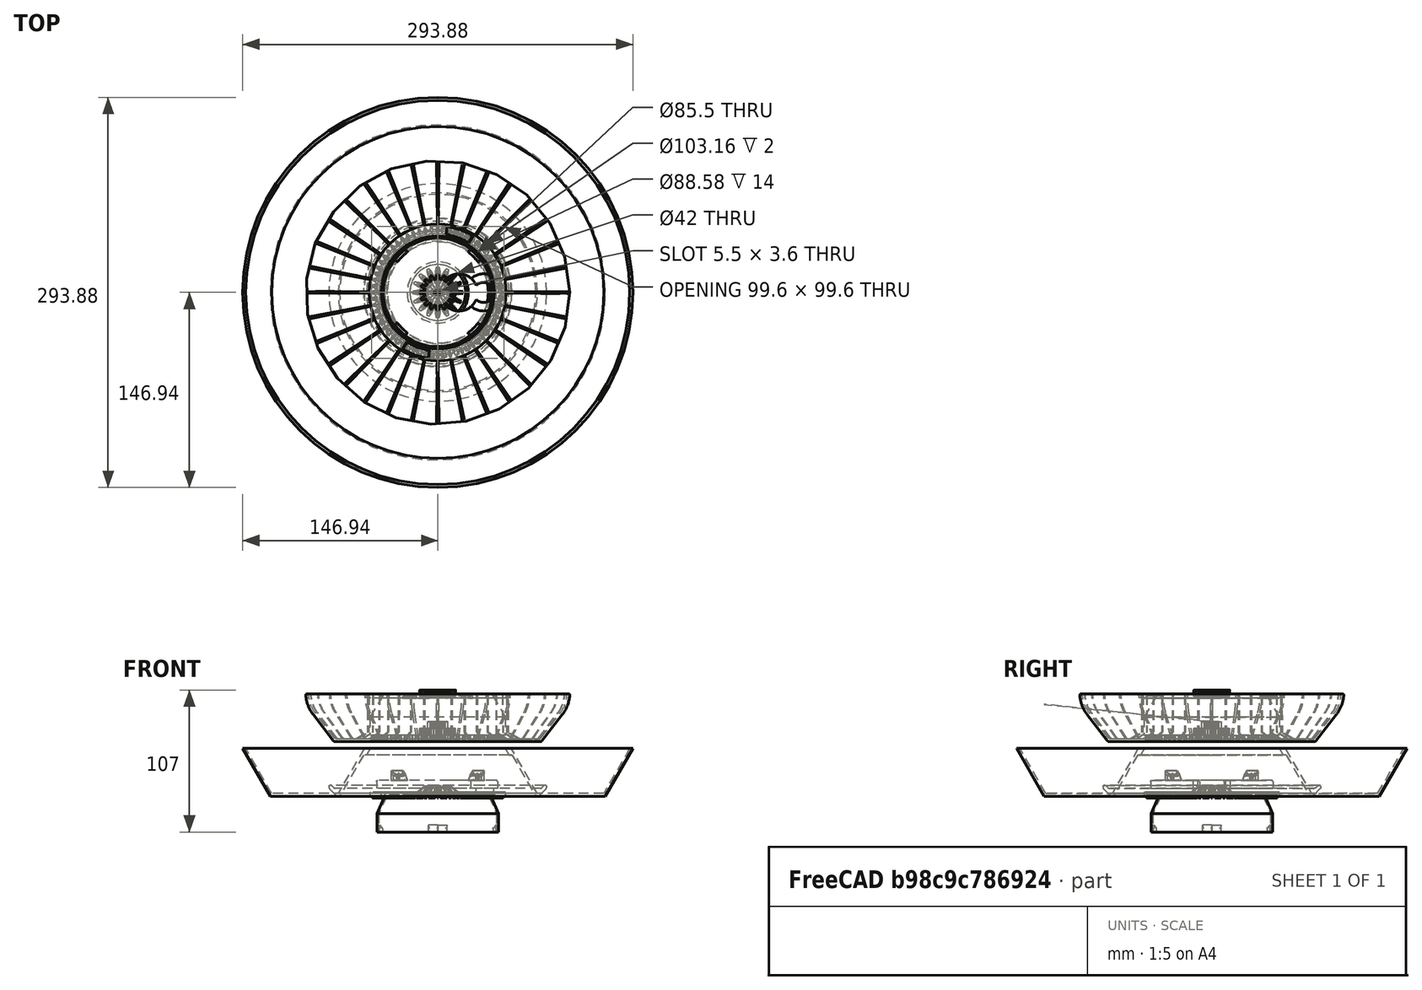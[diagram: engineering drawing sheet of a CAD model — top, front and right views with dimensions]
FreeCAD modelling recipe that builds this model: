
FCSTD DOCUMENT  (FreeCAD 1.1R43087 (Git))
Label: smart_medication_box
License: All rights reserved
LicenseURL: https://en.wikipedia.org/wiki/All_rights_reserved
objects: Sketcher::SketchObject×22, PartDesign::Fillet×13, App::Point×12, PartDesign::Body×11, PartDesign::Pocket×7, PartDesign::Revolution×7, Part::DatumPlane×6, PartDesign::Pad×6, App::Link×6, PartDesign::PolarPattern×5, Measure::MeasureRadius×5, Part::FeaturePython×4, App::FeaturePython×4, Measure::MeasureDistance×4, PartDesign::FeaturePython×3, PartDesign::FeatureBase×2, Mesh::Feature×2, Part::Feature×2, App::VarSet×1, PartDesign::AdditivePipe×1, +8 more types
note: 189 computed .brp shape members not serialized (recipe doc carries the construction recipe); baked Part::Feature solids carry a one-line shape summary decoded from their .brp

FEATURE [App::Point] Origin001
  Role = Origin
FEATURE [Sketcher::SketchObject] Sketch001
  ArcFitTolerance = 1e-06
  ExternalTypes = [0]
  FullyConstrained = true
  MakeInternals = false
  MapMode = 5
  Placement = pos=(0,0,0) rot=(1,0,0;3.14159rad)
  expr: Constraints[10] = 3.1
  expr: Constraints[11] = 2.6
  sketch-geometry (4):
    g0: LineSegment StartX=-1.55 StartY=2.08746 StartZ=0 EndX=-1.55 EndY=-2.08746 EndZ=0
    g1: LineSegment StartX=1.55 StartY=2.08746 StartZ=0 EndX=1.55 EndY=-2.08746 EndZ=0
    g2: ArcOfCircle CenterX=0 CenterY=0 CenterZ=0 NormalX=0 NormalY=0 NormalZ=1 AngleXU=0 Radius=2.6 StartAngle=0.932094 EndAngle=2.2095
    g3: ArcOfCircle CenterX=0 CenterY=0 CenterZ=0 NormalX=0 NormalY=0 NormalZ=1 AngleXU=0 Radius=2.6 StartAngle=4.07369 EndAngle=5.35109
  constraints (12):
    c: Vertical(g1)
    c: Coincident(g2,g-1)
    c: Coincident(g2,g0)
    c: Coincident(g2,g1)
    c: Coincident(g3,g2)
    c: Coincident(g3,g0)
    c: Coincident(g3,g1)
    c: Parallel(g1,g0)
    c: Equal(g1,g0)
    c: Equal(g2,g3)
    c: Distance(g0,g1) = 3.1
    c: Radius(g2) = 2.6
FEATURE [Part::FeaturePython] BevelGear  # WARN: FeaturePython — macro-defined, semantics opaque (R4)
  AttacherType = Attacher::AttachEngine3D
  angular_backlash = 0
  backlash = 0
  beta = 0
  clearance = 0.1
  dw = 32
  height = 7.5
  module = 2
  num_teeth = 16
  numpoints = 20
  pitch_angle = 45
  pressure_angle = 20
  reset_origin = true
  version = 1.3.0
  expr: angular_backlash = backlash / dw * 360 ° / pi
  expr: dw = num_teeth * module
  expr: height = 7.5
  expr: module = 2
  expr: num_teeth = 16
FEATURE [PartDesign::FeatureBase] BaseFeature
  BaseFeature = -> BevelGear
  Suppressed = false
FEATURE [PartDesign::Pocket] Pocket
  BaseFeature = -> BaseFeature
  Direction = (0,0,1)
  Length = 6
  Length2 = 5
  Profile = -> Sketch001
  ReferenceAxis = -> Sketch001 [N_Axis]
  Refine = true
  SideType = 0
  Suppressed = false
  Type = 0
  Type2 = 0
  expr: Length = 6
FEATURE [PartDesign::Body] Body  label="stepper_gear"
  AllowCompound = false
  BaseFeature = -> BevelGear
  Group = -> [BaseFeature,Sketch001,Pocket]
  Origin = -> Origin
  Tip = -> Pocket
FEATURE [App::Point] Origin003
  Role = Origin
FEATURE [Sketcher::SketchObject] Sketch
  ArcFitTolerance = 1e-06
  AttachmentSupport = -> [Origin002]
  ExternalTypes = [0]
  FullyConstrained = true
  MakeInternals = false
  MapMode = 5
  expr: Constraints[1] = 2 * VarSet.outer_ring_center_radius
  sketch-geometry (1):
    g0: Circle CenterX=0 CenterY=0 CenterZ=0 NormalX=0 NormalY=0 NormalZ=1 AngleXU=0 Radius=100
  constraints (2):
    c: Coincident(g0,g-1)
    c: Diameter(g0) = 200
FEATURE [App::VarSet] VarSet
  fillet_oouter_gear = 0.8
  outer_gear_section_length = 48
  outer_ring_bottom_width = 50
  outer_ring_center_radius = 100
  outer_ring_height = 36
  outer_ring_sides_angle = 30
  outer_wall_thickness = 2
  wall_thickness = 2
  expr: fillet_oouter_gear = 0.8
  expr: outer_ring_bottom_width = 50
  expr: outer_ring_center_radius = 100
  expr: outer_ring_height = 36
  expr: outer_ring_sides_angle = 30
FEATURE [Part::DatumPlane] DatumPlane
  AttachmentSupport = -> [Sketch]
  MapMode = 7
  Placement = pos=(100,0,0) rot=(1,0,0;1.5708rad)
FEATURE [Sketcher::SketchObject] Sketch002
  ArcFitTolerance = 1e-06
  AttachmentSupport = -> [DatumPlane]
  ExternalTypes = [0]
  FullyConstrained = true
  MakeInternals = false
  MapMode = 5
  Placement = pos=(100,0,0) rot=(1,0,0;1.5708rad)
  expr: Constraints[13] = VarSet.outer_ring_height
  expr: Constraints[16] = VarSet.outer_ring_sides_angle
  expr: Constraints[17] = VarSet.outer_ring_sides_angle
  expr: Constraints[19] = 5
  expr: Constraints[21] = VarSet.wall_thickness * 2
  expr: Constraints[24] = VarSet.wall_thickness
  expr: Constraints[28] = VarSet.outer_ring_bottom_width
  expr: Constraints[7] = VarSet.wall_thickness
  expr: Constraints[8] = VarSet.outer_ring_height
  expr: Constraints[9] = VarSet.wall_thickness
  sketch-geometry (10):
    g0: LineSegment StartX=26.1547 StartY=0 StartZ=0 EndX=46.9393 EndY=36 EndZ=0
    g1: LineSegment StartX=46.9393 StartY=36 StartZ=0 EndX=44.6299 EndY=36 EndZ=0
    g2: LineSegment StartX=44.6299 StartY=36 StartZ=0 EndX=25 EndY=2 EndZ=0
    g3: LineSegment StartX=25 StartY=2 StartZ=0 EndX=-25 EndY=2 EndZ=0
    g4: LineSegment StartX=-25 StartY=2 StartZ=0 EndX=-44.6299 EndY=36 EndZ=0
    g5: LineSegment StartX=-44.6299 StartY=36 StartZ=0 EndX=-49.2487 EndY=36 EndZ=0
    g6: LineSegment StartX=-26.1547 StartY=0 StartZ=0 EndX=26.1547 EndY=0 EndZ=0
    g7: LineSegment StartX=-49.2487 StartY=36 StartZ=0 EndX=-46.362 EndY=31 EndZ=0
    g8: LineSegment StartX=-44.0526 StartY=31 StartZ=0 EndX=-26.1547 EndY=0 EndZ=0
    g9: LineSegment StartX=-44.0526 StartY=31 StartZ=0 EndX=-46.362 EndY=31 EndZ=0
  constraints (29):
    c: Coincident(g1,g0)
    c: Coincident(g1,g2)
    c: Coincident(g2,g3)
    c: Coincident(g3,g4)
    c: Coincident(g4,g5)
    c: Horizontal(g5)
    c: Coincident(g6,g0)
    c: Distance(g0,g2) = 2
    c: DistanceY(g6,g4) = 36
    c: DistanceY(g6,g3) = 2
    c: Parallel(g3,g6)
    c: Parallel(g1,g-1)
    c: Parallel(g0,g2)
    c: Distance(g-1,g1) = 36
    c: Symmetric(g6,g0,g-2)
    c: PointOnObject(g0,g-1)
    c: Angle(g2,g-2) = 0.523599
    c: Angle(g-2,g4) = 0.523599
    c: Coincident(g7,g5)
    c: DistanceY(g7,g5) = 5
    c: Parallel(g7,g4)
    c: Distance(g4,g7) = 4
    c: Coincident(g8,g6)
    c: Parallel(g8,g4)
    c: Distance(g4,g8) = 2
    c: Coincident(g9,g8)
    c: Coincident(g9,g7)
    c: Parallel(g9,g5)
    c: DistanceX(g3,g3) = 50
FEATURE [PartDesign::AdditivePipe] AdditivePipe
  AuxiliaryCurvilinear = true
  AuxiliarySpineTangent = false
  Binormal = (0,0,0)
  Mode = 0
  Placement = pos=(100,0,0) rot=(1,0,0;1.5708rad)
  Profile = -> Sketch002
  Refine = true
  Spine = -> Sketch
  SpineTangent = false
  Suppressed = false
  Transformation = 0
  Transition = 0
FEATURE [PartDesign::Body] Body001  label="outer_sections_ring_gear"
  AllowCompound = false
  Group = -> [Sketch,DatumPlane,Sketch002,AdditivePipe]
  Origin = -> Origin002
  Tip = -> AdditivePipe
FEATURE [App::Point] Origin005
  Role = Origin
FEATURE [PartDesign::FeaturePython] BevelGear001  # WARN: FeaturePython — macro-defined, semantics opaque (R4)
  AttacherType = Attacher::AttachEngine3D
  Suppressed = false
  angular_backlash = 0
  backlash = 0
  beta = 0
  clearance = 0.1
  dw = 96
  height = 5
  module = 1.5
  num_teeth = 64
  numpoints = 20
  pitch_angle = 30
  pressure_angle = 20
  reset_origin = true
  version = 1.3.0
  expr: angular_backlash = backlash / dw * 360 ° / pi
  expr: dw = num_teeth * module
  expr: module = 1.5
  expr: num_teeth = 64
  expr: pitch_angle = 30
FEATURE [PartDesign::Body] Body002  label="Body"
  AllowCompound = false
  Group = -> [BevelGear001]
  Origin = -> Origin004
  Placement = pos=(0,0,45) rot=(0,0,1;0rad)
  Tip = -> BevelGear001
FEATURE [Part::Cut] Cut
  Base = -> Body001
  Refine = true
  Tool = -> Body002
FEATURE [App::Point] Origin007
  Role = Origin
FEATURE [Sketcher::SketchObject] Sketch003
  ArcFitTolerance = 1e-06
  AttachmentSupport = -> [Origin006]
  ExternalTypes = [0]
  FullyConstrained = true
  MakeInternals = false
  MapMode = 5
  expr: Constraints[0] = 53 * 2
  sketch-geometry (1):
    g0: Circle CenterX=0 CenterY=0 CenterZ=0 NormalX=0 NormalY=0 NormalZ=1 AngleXU=0 Radius=53
  constraints (2):
    c: Diameter(g0) = 106
    c: Coincident(g0,g-1)
FEATURE [PartDesign::Pad] Pad
  Direction = (0,0,1)
  Length = 6
  Length2 = 10
  Profile = -> Sketch003
  ReferenceAxis = -> Sketch003 [N_Axis]
  Refine = true
  SideType = 0
  Suppressed = false
  Type = 0
  Type2 = 0
  expr: Length = 6
FEATURE [Sketcher::SketchObject] Sketch004
  ArcFitTolerance = 1e-06
  AttachmentSupport = -> [Pad]
  ExternalTypes = [0]
  FullyConstrained = true
  MakeInternals = false
  MapMode = 5
  Placement = pos=(0,0,6) rot=(0,0,1;0rad)
  expr: Constraints[0] = 48 * 2 - 4
  sketch-geometry (1):
    g0: Circle CenterX=0 CenterY=0 CenterZ=0 NormalX=0 NormalY=0 NormalZ=1 AngleXU=0 Radius=46
  constraints (2):
    c: Diameter(g0) = 92
    c: Coincident(g0,g-1)
FEATURE [PartDesign::Pad] Pad001
  BaseFeature = -> Pad
  Direction = (0,0,1)
  Length = 6
  Length2 = 10
  Profile = -> Sketch004
  ReferenceAxis = -> Sketch004 [N_Axis]
  Refine = true
  SideType = 0
  Suppressed = false
  Type = 0
  Type2 = 0
  expr: Length = 6
FEATURE [Part::FeaturePython] InvoluteGear  # WARN: FeaturePython — macro-defined, semantics opaque (R4)
  AttacherType = Attacher::AttachEngine3D
  Placement = pos=(0,0,41) rot=(0,0,1;0rad)
  addendum_diameter = 15
  angular_backlash = 0
  axle_hole = false
  axle_holesize = 10
  backlash = 0
  clearance = 0.25
  double_helix = false
  head = 0
  head_fillet = 0
  height = 5
  helix_angle = 0
  module = 1.5
  num_teeth = 8
  numpoints = 20
  offset_hole = false
  offset_holeoffset = 10
  offset_holesize = 10
  pitch_diameter = 12
  pressure_angle = 20
  properties_from_tool = false
  reversed_backlash = false
  root_diameter = 8.25
  root_fillet = 0
  shift = 0
  simple = false
  transverse_pitch = 4.71239
  traverse_module = 1.5
  undercut = false
  version = 1.3.0
  expr: angular_backlash = backlash / pitch_diameter * 360 ° / pi
  expr: module = 1.5
  expr: num_teeth = 8
FEATURE [Sketcher::SketchObject] Sketch005
  ArcFitTolerance = 1e-06
  AttachmentSupport = -> [Pad001]
  ExternalGeometry = -> [Pad001]
  ExternalTypes = [0]
  FullyConstrained = true
  MakeInternals = false
  MapMode = 5
  Placement = pos=(0,0,12) rot=(0,0,1;0rad)
  expr: Constraints[0] = 28
  expr: Constraints[4] = 11.5
  sketch-geometry (2):
    g0: Circle CenterX=34.5 CenterY=0 CenterZ=0 NormalX=0 NormalY=0 NormalZ=1 AngleXU=0 Radius=14
    g1: Circle [constr] CenterX=34.5 CenterY=0 CenterZ=0 NormalX=0 NormalY=0 NormalZ=1 AngleXU=0 Radius=11.5
  constraints (5):
    c: Diameter(g0) = 28
    c: Coincident(g1,g0)
    c: Tangent(g1,g-3)
    c: PointOnObject(g0,g-1)
    c: Distance(g0,g-3) = 11.5
FEATURE [PartDesign::Pocket] Pocket001
  BaseFeature = -> Pad001
  Direction = (0,0,-1)
  Length = 6
  Length2 = 5
  Profile = -> Sketch005
  ReferenceAxis = -> Sketch005 [N_Axis]
  Refine = true
  SideType = 0
  Suppressed = false
  Type = 0
  Type2 = 0
  expr: Length = 6
FEATURE [Sketcher::SketchObject] Sketch006
  ArcFitTolerance = 1e-06
  AttachmentSupport = -> [Pocket001]
  ExternalGeometry = -> [Pocket001]
  ExternalTypes = [0,0]
  FullyConstrained = true
  MakeInternals = false
  MapMode = 5
  Placement = pos=(0,0,6) rot=(0,0,1;0rad)
  sketch-geometry (1):
    g0: Circle CenterX=34.5 CenterY=0 CenterZ=0 NormalX=0 NormalY=0 NormalZ=1 AngleXU=0 Radius=7.6
  constraints (2):
    c: Diameter(g0) = 15.2
    c: Coincident(g0,g-4)
FEATURE [PartDesign::Pocket] Pocket002
  BaseFeature = -> Pocket001
  Direction = (0,0,-1)
  Length = 5
  Length2 = 5
  Profile = -> Sketch006
  ReferenceAxis = -> Sketch006 [N_Axis]
  Refine = true
  SideType = 0
  Suppressed = false
  Type = 0
  Type2 = 0
FEATURE [App::Point] Origin011
  Role = Origin
FEATURE [PartDesign::FeaturePython] InvoluteGear001  # WARN: FeaturePython — macro-defined, semantics opaque (R4)
  AttacherType = Attacher::AttachEngine3D
  Suppressed = false
  addendum_diameter = 27
  angular_backlash = 0
  axle_hole = false
  axle_holesize = 10
  backlash = 0
  clearance = 0.25
  double_helix = false
  head = 0
  head_fillet = 0
  height = 5
  helix_angle = 0
  module = 1.5
  num_teeth = 16
  numpoints = 20
  offset_hole = false
  offset_holeoffset = 10
  offset_holesize = 10
  pitch_diameter = 24
  pressure_angle = 20
  properties_from_tool = false
  reversed_backlash = false
  root_diameter = 20.25
  root_fillet = 0
  shift = 0
  simple = false
  transverse_pitch = 4.71239
  traverse_module = 1.5
  undercut = false
  version = 1.3.0
  expr: angular_backlash = backlash / pitch_diameter * 360 ° / pi
  expr: module = 1.5
  expr: num_teeth = 16
FEATURE [Sketcher::SketchObject] Sketch007
  ArcFitTolerance = 1e-06
  AttachmentSupport = -> [Pocket002]
  ExternalGeometry = -> [Pocket002]
  ExternalTypes = [0]
  FullyConstrained = true
  MakeInternals = false
  MapMode = 5
  Placement = pos=(0,0,12) rot=(0,0,1;0rad)
  expr: Constraints[0] = 28
  expr: Constraints[2] = -3
  sketch-geometry (1):
    g0: Circle CenterX=15.9 CenterY=0 CenterZ=0 NormalX=0 NormalY=0 NormalZ=1 AngleXU=0 Radius=14
  constraints (3):
    c: Diameter(g0) = 28
    c: PointOnObject(g0,g-1)
    c: Distance(g0,g-3) = -3
FEATURE [PartDesign::Pocket] Pocket003
  BaseFeature = -> Pocket002
  Direction = (0,0,-1)
  Length = 11
  Length2 = 5
  Profile = -> Sketch007
  ReferenceAxis = -> Sketch007 [N_Axis]
  Refine = true
  SideType = 0
  Suppressed = false
  Type = 0
  Type2 = 0
  expr: Length = 11
FEATURE [Sketcher::SketchObject] Sketch008
  ArcFitTolerance = 1e-06
  AttachmentSupport = -> [InvoluteGear001]
  ExternalTypes = [0]
  FullyConstrained = true
  MakeInternals = false
  MapMode = 5
  Placement = pos=(0,0,5) rot=(0,0,1;0rad)
  expr: Constraints[11] = 3.1
  sketch-geometry (4):
    g0: ArcOfCircle CenterX=0 CenterY=0 CenterZ=0 NormalX=0 NormalY=0 NormalZ=1 AngleXU=0 Radius=2.5 StartAngle=2.47285 EndAngle=3.81034
    g1: ArcOfCircle CenterX=0 CenterY=0 CenterZ=0 NormalX=0 NormalY=0 NormalZ=1 AngleXU=0 Radius=2.5 StartAngle=5.61444 EndAngle=6.95193
    g2: LineSegment StartX=-1.9615 StartY=1.55 StartZ=0 EndX=1.9615 EndY=1.55 EndZ=0
    g3: LineSegment StartX=1.9615 StartY=-1.55 StartZ=0 EndX=-1.9615 EndY=-1.55 EndZ=0
  constraints (12):
    c: Coincident(g0,g-1)
    c: Coincident(g0,g1)
    c: Diameter(g0) = 5
    c: Equal(g1,g0)
    c: Coincident(g2,g0)
    c: Coincident(g2,g1)
    c: Coincident(g3,g1)
    c: Coincident(g3,g0)
    c: Parallel(g3,g2)
    c: Parallel(g-1,g2)
    c: Equal(g2,g3)
    c: Distance(g3,g2) = 3.1
FEATURE [PartDesign::Pocket] Pocket004
  BaseFeature = -> InvoluteGear001
  Direction = (0,0,-1)
  Length = 5
  Length2 = 5
  Profile = -> Sketch008
  ReferenceAxis = -> Sketch008 [N_Axis]
  Refine = true
  SideType = 0
  Suppressed = false
  Type = 0
  Type2 = 0
FEATURE [App::Link] Body006  label="base"
  LinkedObject = -> Body003
FEATURE [App::Point] Origin013
  Role = Origin
FEATURE [Part::FeaturePython] InvoluteGear002  # WARN: FeaturePython — macro-defined, semantics opaque (R4)
  AttacherType = Attacher::AttachEngine3D
  Placement = pos=(0,0,46) rot=(0,0,1;0rad)
  addendum_diameter = 27
  angular_backlash = 0
  axle_hole = false
  axle_holesize = 10
  backlash = 0
  clearance = 0.25
  double_helix = false
  head = 0
  head_fillet = 0
  height = 5
  helix_angle = 0
  module = 1.5
  num_teeth = 16
  numpoints = 20
  offset_hole = false
  offset_holeoffset = 10
  offset_holesize = 10
  pitch_diameter = 24
  pressure_angle = 20
  properties_from_tool = false
  reversed_backlash = false
  root_diameter = 20.25
  root_fillet = 0
  shift = 0
  simple = false
  transverse_pitch = 4.71239
  traverse_module = 1.5
  undercut = false
  version = 1.3.0
  expr: angular_backlash = backlash / pitch_diameter * 360 ° / pi
  expr: module = 1.5
FEATURE [App::Point] Origin027
  Role = Origin
FEATURE [PartDesign::FeaturePython] InternalInvoluteGear  # WARN: FeaturePython — macro-defined, semantics opaque (R4)
  AttacherType = Attacher::AttachEngine3D
  Suppressed = false
  addendum_diameter = 94.2
  angular_backlash = 0
  backlash = 0
  clearance = 0.2
  double_helix = false
  head = -0.4
  head_fillet = 0
  height = 5
  helix_angle = 0
  module = 1.5
  num_teeth = 64
  numpoints = 20
  outside_diameter = 106
  pitch_diameter = 96
  pressure_angle = 20
  properties_from_tool = false
  reversed_backlash = false
  root_diameter = 99.6
  root_fillet = 0
  shift = 0
  simple = false
  thickness = 5
  transverse_pitch = 4.71239
  version = 1.3.0
  expr: angular_backlash = backlash / pitch_diameter * 360 ° / pi
  expr: clearance = 0.2
  expr: module = 1.5
  expr: num_teeth = 64
  expr: pressure_angle = 20
FEATURE [App::Point] Origin029
  Role = Origin
FEATURE [PartDesign::FeatureBase] BaseFeature002
  BaseFeature = -> InvoluteGear002
  Suppressed = false
FEATURE [PartDesign::Body] Body017
  AllowCompound = false
  BaseFeature = -> InvoluteGear002
  Group = -> [BaseFeature002]
  Origin = -> Origin028
  Placement = pos=(0,0,46) rot=(0,0,1;0rad)
  Tip = -> BaseFeature002
FEATURE [Part::FeaturePython] InvoluteGear003  # WARN: FeaturePython — macro-defined, semantics opaque (R4)
  AttacherType = Attacher::AttachEngine3D
  Placement = pos=(0,0,51) rot=(0,0,1;0rad)
  addendum_diameter = 15
  angular_backlash = 0
  axle_hole = false
  axle_holesize = 10
  backlash = 0
  clearance = 0.25
  double_helix = false
  head = 0
  head_fillet = 0
  height = 5
  helix_angle = 0
  module = 1.5
  num_teeth = 8
  numpoints = 20
  offset_hole = false
  offset_holeoffset = 10
  offset_holesize = 10
  pitch_diameter = 12
  pressure_angle = 20
  properties_from_tool = false
  reversed_backlash = false
  root_diameter = 8.25
  root_fillet = 0
  shift = 0
  simple = false
  transverse_pitch = 4.71239
  traverse_module = 1.5
  undercut = false
  version = 1.3.0
  expr: angular_backlash = backlash / pitch_diameter * 360 ° / pi
  expr: module = 1.5
  expr: num_teeth = 8
FEATURE [App::Point] Origin031
  Role = Origin
FEATURE [PartDesign::Boolean] Boolean
  Group = -> [InvoluteGear003,InvoluteGear002,Body017]
  Suppressed = false
  Type = 0
  UsePlacement = true
FEATURE [App::Link] Body019  label="middle_gear"
  LinkPlacement = pos=(34.5001,5.70397e-05,57) rot=(0.896948,-0.442137,0;3.14159rad)
  LinkedObject = -> Body018
  Placement = pos=(34.5001,5.70397e-05,57) rot=(0.896948,-0.442137,0;3.14159rad)
FEATURE [App::Link] motor_gear001
  LinkPlacement = pos=(48.7587,22.5689,48.2418) rot=(0,0,1;3.81033rad)
  LinkedObject = -> Body005
  Placement = pos=(48.7587,22.5689,48.2418) rot=(0,0,1;3.81033rad)
FEATURE [App::Link] outer_gear
  LinkPlacement = pos=(-51.3171,169.82,65.8237) rot=(0,0,1;2.25636rad)
  LinkedObject = -> Body016
  Placement = pos=(-51.3171,169.82,65.8237) rot=(0,0,1;2.25636rad)
FEATURE [Part::DatumPlane] DatumPlane001
  AttachmentSupport = -> [Pocket003]
  MapMode = 7
  Placement = pos=(53,0,0) rot=(1,0,0;1.5708rad)
FEATURE [Sketcher::SketchObject] Sketch009
  ArcFitTolerance = 1e-06
  AttachmentSupport = -> [DatumPlane001]
  ExternalTypes = [0]
  FullyConstrained = false
  MakeInternals = false
  MapMode = 5
  Placement = pos=(53,0,0) rot=(1,0,0;1.5708rad)
  expr: Constraints[12] = 2
  expr: Constraints[2] = 6
  expr: Constraints[4] = 25
  sketch-geometry (17):
    g0: LineSegment StartX=0 StartY=0 StartZ=0 EndX=0 EndY=6 EndZ=0
    g1: LineSegment StartX=0 StartY=6 StartZ=0 EndX=24.3276 EndY=6 EndZ=0
    g2: LineSegment StartX=25.4755 StartY=6.47549 StartZ=0 EndX=26.6668 EndY=7.66678 EndZ=0
    g3: LineSegment StartX=27.4713 StartY=8 StartZ=0 EndX=28.4345 EndY=8 EndZ=0
    g4: LineSegment StartX=29 StartY=7.43449 StartZ=0 EndX=29 EndY=6.73331 EndZ=0
    g5: LineSegment StartX=28.4815 StartY=5.48147 StartZ=0 EndX=23.8351 EndY=0.835147 EndZ=0
    g6: LineSegment StartX=0 StartY=0 StartZ=0 EndX=21.8189 EndY=0 EndZ=0
    g7: ArcOfCircle CenterX=28.4345 CenterY=7.43449 CenterZ=0 NormalX=0 NormalY=0 NormalZ=1 AngleXU=0 Radius=0.565506 StartAngle=0 EndAngle=1.5708
    g8: GeomPoint [constr] X=29 Y=8 Z=0
    g9: ArcOfCircle CenterX=27.4713 CenterY=6.8623 CenterZ=0 NormalX=0 NormalY=0 NormalZ=1 AngleXU=0 Radius=1.1377 StartAngle=1.5708 EndAngle=2.35619
    g10: GeomPoint [constr] X=27 Y=8 Z=0
    g11: ArcOfCircle CenterX=27.2296 CenterY=6.73331 CenterZ=0 NormalX=0 NormalY=0 NormalZ=1 AngleXU=0 Radius=1.77037 StartAngle=5.49779 EndAngle=6.28319
    g12: GeomPoint [constr] X=29 Y=6 Z=0
    g13: ArcOfCircle CenterX=24.3276 CenterY=7.62341 CenterZ=0 NormalX=0 NormalY=0 NormalZ=1 AngleXU=0 Radius=1.62341 StartAngle=4.71239 EndAngle=5.49779
    g14: GeomPoint [constr] X=25 Y=6 Z=0
    g15: ArcOfCircle CenterX=21.8189 CenterY=2.85137 CenterZ=0 NormalX=0 NormalY=0 NormalZ=1 AngleXU=0 Radius=2.85137 StartAngle=4.71239 EndAngle=5.49779
    g16: GeomPoint [constr] X=23 Y=0 Z=0
  constraints (33):
    c: Coincident(g-1,g0)
    c: Coincident(g0,g1)
    c: Distance(g0,g0) = 6
    c: PointOnObject(g0,g-2)
    c: DistanceX(g1,g14) = 25
    c: PointOnObject(g16,g-1)
    c: Coincident(g6,g0)
    c: Parallel(g2,g5)
    c: Parallel(g1,g6)
    c: Parallel(g3,g1)
    c: Perpendicular(g3,g4)
    c: PointOnObject(g12,g1)
    c: DistanceY(g12,g8) = 2
    c: PointOnObject(g8,g3)
    c: PointOnObject(g8,g4)
    c: Tangent(g3,g7) = 1.5708
    c: Tangent(g4,g7) = 1.5708
    c: PointOnObject(g10,g2)
    c: PointOnObject(g10,g3)
    c: Tangent(g2,g9) = 1.5708
    c: Tangent(g3,g9) = 1.5708
    c: PointOnObject(g12,g5)
    c: PointOnObject(g12,g4)
    c: Tangent(g5,g11) = 1.5708
    c: Tangent(g4,g11) = 1.5708
    c: PointOnObject(g14,g2)
    c: PointOnObject(g14,g1)
    c: Tangent(g2,g13) = -1.5708
    c: Tangent(g1,g13) = -1.5708
    c: PointOnObject(g16,g5)
    c: PointOnObject(g16,g6)
    c: Tangent(g5,g15) = 1.5708
    c: Tangent(g6,g15) = -1.5708
FEATURE [PartDesign::Revolution] Revolution
  Angle = 360
  Angle2 = 60
  Axis = (1e-16,1e-16,1)
  Base = (0,0,0)
  BaseFeature = -> Pocket003
  Profile = -> Sketch009
  ReferenceAxis = -> Z_Axis003
  Refine = true
  Reversed = true
  Suppressed = false
  Type = 0
FEATURE [Part::DatumPlane] DatumPlane002
  AttachmentSupport = -> [InternalInvoluteGear]
  MapMode = 7
  Placement = pos=(53,0,0) rot=(1,0,0;1.5708rad)
FEATURE [Sketcher::SketchObject] Sketch010
  ArcFitTolerance = 1e-06
  AttachmentSupport = -> [DatumPlane002]
  ExternalGeometry = -> [InternalInvoluteGear]
  ExternalTypes = [0]
  FullyConstrained = false
  MakeInternals = false
  MapMode = 5
  Placement = pos=(53,0,0) rot=(1,0,0;1.5708rad)
  expr: Constraints[10] = VarSet.outer_wall_thickness
  expr: Constraints[11] = VarSet.outer_wall_thickness
  expr: Constraints[14] = VarSet.outer_wall_thickness
  expr: Constraints[17] = VarSet.fillet_oouter_gear
  expr: Constraints[2] = 5
  expr: Constraints[34] = VarSet.outer_wall_thickness
  expr: Constraints[36] = VarSet.outer_ring_height
  expr: Constraints[37] = VarSet.fillet_oouter_gear
  expr: Constraints[38] = 30
  expr: Constraints[45] = VarSet.fillet_oouter_gear
  expr: Constraints[50] = 25
  expr: Constraints[52] = 10
  expr: Constraints[6] = 25
  expr: Constraints[9] = VarSet.outer_wall_thickness
  sketch-geometry (28):
    g0: LineSegment StartX=0 StartY=0 StartZ=0 EndX=0 EndY=5 EndZ=0
    g1: LineSegment StartX=0 StartY=0 StartZ=0 EndX=24.0192 EndY=0 EndZ=0
    g2: LineSegment StartX=25.6005 StartY=0.775418 StartZ=0 EndX=40.7862 EndY=20.3842 EndZ=0
    g3: LineSegment StartX=24.6198 StartY=2.77542 StartZ=0 EndX=39.2049 EndY=21.6088 EndZ=0
    g4: LineSegment StartX=9.57963 StartY=2 StartZ=0 EndX=23.0385 EndY=2 EndZ=0
    g5: LineSegment StartX=0 StartY=5 StartZ=0 EndX=-2 EndY=5 EndZ=0
    g6: LineSegment StartX=-0.122418 StartY=35.2036 StartZ=0 EndX=4.22e-14 EndY=7.67973 EndZ=0
    g7: LineSegment StartX=8.57963 StartY=2.26795 StartZ=0 EndX=0.399992 EndY=6.99046 EndZ=0
    g8: ArcOfCircle CenterX=0.799992 CenterY=7.68328 CenterZ=0 NormalX=0 NormalY=0 NormalZ=1 AngleXU=0 Radius=0.8 StartAngle=3.14604 EndAngle=4.18879
    g9: ArcOfCircle CenterX=9.57963 CenterY=4 CenterZ=0 NormalX=0 NormalY=0 NormalZ=1 AngleXU=0 Radius=2 StartAngle=4.18879 EndAngle=4.71239
    g10: GeomPoint [constr] X=9.04373 Y=2 Z=0
    g11: ArcOfCircle CenterX=23.0385 CenterY=4 CenterZ=0 NormalX=0 NormalY=0 NormalZ=1 AngleXU=0 Radius=2 StartAngle=4.71239 EndAngle=5.62423
    g12: GeomPoint [constr] X=24.0192 Y=2 Z=0
    g13: ArcOfCircle CenterX=24.0192 CenterY=2 CenterZ=0 NormalX=0 NormalY=0 NormalZ=1 AngleXU=0 Radius=2 StartAngle=4.71239 EndAngle=5.62423
    g14: GeomPoint [constr] X=25 Y=0 Z=0
    g15: GeomPoint [constr] X=29 Y=5.16508 Z=0
    g16: GeomPoint [constr] X=27 Y=5.84896 Z=0
    g17: ArcOfCircle CenterX=-0.92241 CenterY=35.2 CenterZ=0 NormalX=0 NormalY=0 NormalZ=1 AngleXU=0 Radius=0.8 StartAngle=0.00444768 EndAngle=1.5708
    g18: LineSegment StartX=-10.9224 StartY=36 StartZ=0 EndX=-5.92241 EndY=36 EndZ=0
    g19: ArcOfCircle CenterX=19.4391 CenterY=36.916 CenterZ=0 NormalX=0 NormalY=0 NormalZ=1 AngleXU=0 Radius=27 StartAngle=5.62423 EndAngle=6.21764
    g20: ArcOfCircle CenterX=19.4391 CenterY=36.916 CenterZ=0 NormalX=0 NormalY=0 NormalZ=1 AngleXU=0 Radius=25 StartAngle=5.62423 EndAngle=6.21662
    g21: ArcOfCircle CenterX=45.1819 CenterY=35.2 CenterZ=0 NormalX=0 NormalY=0 NormalZ=1 AngleXU=0 Radius=0.8 StartAngle=1.5708 EndAngle=3.07503
    g22: LineSegment StartX=45.5828 StartY=36 StartZ=0 EndX=45.1819 EndY=36 EndZ=0
    g23: ArcOfCircle CenterX=45.5828 CenterY=35.2 CenterZ=0 NormalX=0 NormalY=0 NormalZ=1 AngleXU=0 Radius=0.8 StartAngle=6.21764 EndAngle=7.85398
    g24: ArcOfCircle CenterX=-10.9224 CenterY=35.2 CenterZ=0 NormalX=0 NormalY=0 NormalZ=1 AngleXU=0 Radius=0.8 StartAngle=1.5708 EndAngle=3.66964
    g25: LineSegment StartX=-11.6134 StartY=34.7969 StartZ=0 EndX=-2.05968 EndY=18.418 EndZ=0
    g26: LineSegment StartX=-2.05968 StartY=18.418 StartZ=0 EndX=-2 EndY=5 EndZ=0
    g27: LineSegment StartX=-5.92241 StartY=36 StartZ=0 EndX=-0.92241 EndY=36 EndZ=0
  constraints (66):
    c: Coincident(g0,g-1)
    c: PointOnObject(g0,g-2)
    c: DistanceY(g0,g0) = 5
    c: Coincident(g1,g0)
    c: PointOnObject(g14,g-1)
    c: Parallel(g3,g2)
    c: DistanceX(g1,g14) = 25
    c: DistanceX(g14,g15) = 4
    c: Parallel(g4,g1)
    c: Distance(g1,g4) = 2
    c: DistanceX(g16,g15) = 2
    c: Distance(g14,g3) = 2
    c: Coincident(g5,g0)
    c: Horizontal(g5)
    c: DistanceX(g5,g5) = 2
    c: Tangent(g8,g7) = 1.5708
    c: Tangent(g8,g6) = -1.5708
    c: Radius(g8) = 0.8
    c: PointOnObject(g6,g-2)
    c: PointOnObject(g10,g7)
    c: PointOnObject(g10,g4)
    c: Tangent(g7,g9) = 1.5708
    c: Tangent(g4,g9) = -1.5708
    c: PointOnObject(g12,g4)
    c: PointOnObject(g12,g3)
    c: Tangent(g4,g11) = -1.5708
    c: Tangent(g3,g11) = -1.5708
    c: PointOnObject(g14,g1)
    c: PointOnObject(g14,g2)
    c: Tangent(g1,g13) = -1.5708
    c: Tangent(g2,g13) = -1.5708
    c: PointOnObject(g15,g2)
    c: PointOnObject(g16,g3)
    c: Equal(g13,g11)
    c: Distance(g0,g8) = 2
    c: Tangent(g17,g6) = 1.5708
    c: Distance(g18,g-1) = 36
    c: Radius(g17) = 0.8
    c: Angle(g7,g1) = 0.523599
    c: Equal(g11,g9)
    c: Coincident(g20,g19)
    c: Tangent(g20,g3) = -1.5708
    c: Tangent(g19,g2) = -1.5708
    c: Tangent(g22,g21) = -1.5708
    c: Tangent(g21,g20) = 1.5708
    c: Radius(g21) = 0.8
    c: Tangent(g23,g22) = -1.5708
    c: Tangent(g23,g19) = -1.5708
    c: Equal(g23,g21)
    c: Parallel(g22,g-1)
    c: Radius(g20) = 25
    c: Radius(g11) = 2
    c: DistanceX(g18,g27) = 10
    c: Tangent(g24,g18) = 1.5708
    c: Equal(g24,g17)
    c: Coincident(g26,g25)
    c: Coincident(g26,g5)
    c: Parallel(g26,g6)
    c: Tangent(g25,g24) = -1.5708
    c: Perpendicular(g-2,g18)
    c: Perpendicular(g-2,g27)
    c: Coincident(g18,g27)
    c: Tangent(g27,g17) = 1.5708
    c: Equal(g27,g18)
    c: Angle(g26,g25) = 0.523599
    c: Vertical(g18,g-3)
FEATURE [PartDesign::Revolution] Revolution001
  Angle = 360
  Angle2 = 60
  Axis = (1e-16,1e-16,1)
  Base = (0,0,0)
  BaseFeature = -> InternalInvoluteGear
  Profile = -> Sketch010
  ReferenceAxis = -> Z_Axis013
  Refine = true
  Reversed = true
  Suppressed = false
  Type = 0
FEATURE [Sketcher::SketchObject] Sketch011
  ArcFitTolerance = 1e-06
  AttachmentSupport = -> [DatumPlane002]
  ExternalGeometry = -> [Revolution001]
  ExternalTypes = [0,0,0,0,0,0,0,0,0]
  FullyConstrained = true
  MakeInternals = false
  MapMode = 5
  Placement = pos=(53,0,0) rot=(1,0,0;1.5708rad)
  sketch-geometry (2):
    g0: LineSegment StartX=-0.92241 StartY=36 StartZ=0 EndX=45.1819 EndY=36 EndZ=0
    g1: LineSegment StartX=9.57963 StartY=2 StartZ=0 EndX=23.0385 EndY=2 EndZ=0
  constraints (4):
    c: Coincident(g0,g-11)
    c: Coincident(g0,g-7)
    c: Tangent(g1,g-6) = -1.5708
    c: Coincident(g1,g-8)
FEATURE [PartDesign::Revolution] Revolution002
  Angle = 1
  Angle2 = 60
  Axis = (1e-16,1e-16,1)
  Base = (0,0,0)
  BaseFeature = -> Revolution001
  Midplane = true
  Profile = -> Sketch011
  ReferenceAxis = -> Z_Axis013
  Refine = true
  Suppressed = false
  Type = 0
  expr: Angle = 1
FEATURE [PartDesign::PolarPattern] PolarPattern
  Angle = 360
  Axis = -> Z_Axis013
  BaseFeature = -> Revolution002
  Mode = 0
  Occurrences = 32
  Offset = 120
  Originals = -> [Revolution002]
  Refine = true
  Suppressed = false
  TransformMode = 0
  expr: Occurrences = 32
FEATURE [PartDesign::Fillet] Fillet
  Base = -> Revolution [Edge27]
  BaseFeature = -> Revolution
  Radius = 1
  Refine = true
  SupportTransform = false
  Suppressed = false
  UseAllEdges = false
FEATURE [PartDesign::Fillet] Fillet001
  Base = -> Boolean [Face4]
  BaseFeature = -> Boolean
  Radius = 0.25
  Refine = true
  SupportTransform = false
  Suppressed = false
  UseAllEdges = false
  expr: Radius = 0.25
FEATURE [PartDesign::Fillet] Fillet002
  Base = -> Fillet001 [Face4,Face243]
  BaseFeature = -> Fillet001
  Radius = 0.2
  Refine = true
  SupportTransform = false
  Suppressed = false
  UseAllEdges = false
  expr: Radius = 0.2
FEATURE [PartDesign::Body] Body018
  AllowCompound = false
  Group = -> [Boolean,Fillet001,Fillet002]
  Origin = -> Origin030
  Tip = -> Fillet002
FEATURE [PartDesign::Body] Body020  label="upper_cover"
  AllowCompound = false
  Origin = -> Origin032
FEATURE [App::Point] Origin033
  Role = Origin
FEATURE [Mesh::Feature] Round_Display_shell_3D_Model_stl_B  label="Round-Display-shell-3D-Model.stl_B"
FEATURE [Part::Feature] Round_Display_shell_3D_Model_stl_B001
  shape: large baked B-rep (50 MB .brp); summary skipped
FEATURE [App::FeaturePython] Motion001  label="Revolute (Angular)"  # WARN: FeaturePython — macro-defined, semantics opaque (R4)
  Formula = 5*time
  MotionType = 0
FEATURE [App::FeaturePython] Simulation001  # WARN: FeaturePython — macro-defined, semantics opaque (R4)
  Group = -> [Motion001]
  aTimeStart = 0
  bTimeEnd = 3
  cTimeStepOutput = 0.01
  fGlobalErrorTolerance = 1e-06
  jFramesPerSecond = 30
FEATURE [Assembly::SimulationGroup] Simulations
  Group = -> [Simulation001]
FEATURE [Mesh::Feature] Round_Display_shell_3D_Model_stl_A  label="Round-Display-shell-3D-Model.stl_A"
FEATURE [Part::Feature] Round_Display_shell_3D_Model_stl_A001
  shape: large baked B-rep (46 MB .brp); summary skipped
FEATURE [Measure::MeasureDistance] Distance001  label="Distance001: 36.99 mm"
  Distance = 36.9884
  DistanceX = 11.811
  DistanceY = 35.052
  DistanceZ = 1.04904e-05
  Element1 = -> Round_Display_shell_3D_Model_stl_A001 [Vertex28685]
  Element2 = -> Round_Display_shell_3D_Model_stl_A001 [Vertex28897]
  Position1 = (262.292,164.85,-8.34998)
  Position2 = (274.103,129.798,-8.34999)
FEATURE [App::Point] Origin035
  Role = Origin
FEATURE [Sketcher::SketchObject] Sketch012
  ArcFitTolerance = 1e-06
  AttachmentSupport = -> [Origin034]
  ExternalTypes = [0]
  FullyConstrained = true
  MakeInternals = false
  MapMode = 5
  expr: Constraints[2] = 80
  sketch-geometry (3):
    g0: Circle CenterX=0 CenterY=0 CenterZ=0 NormalX=0 NormalY=0 NormalZ=1 AngleXU=0 Radius=21
    g1: Circle CenterX=0 CenterY=0 CenterZ=0 NormalX=0 NormalY=0 NormalZ=1 AngleXU=0 Radius=40
    g2: Circle CenterX=0 CenterY=0 CenterZ=0 NormalX=0 NormalY=0 NormalZ=1 AngleXU=0 Radius=38.5
  constraints (6):
    c: Diameter(g0) = 42
    c: Coincident(g0,g-1)
    c: Diameter(g1) = 80
    c: Coincident(g1,g0)
    c: Coincident(g2,g0)
    c: Diameter(g2) = 77
FEATURE [App::Link] upper_cover_display
  LinkPlacement = pos=(115.041,-26.8788,118.586) rot=(0,0,1;0rad)
  LinkedObject = -> Body021
  Placement = pos=(115.041,-26.8788,118.586) rot=(0,0,1;0rad)
FEATURE [Sketcher::SketchObject] Sketch015
  ArcFitTolerance = 1e-06
  AttachmentSupport = -> [PolarPattern]
  ExternalGeometry = -> [PolarPattern]
  ExternalTypes = [0,0,0]
  FullyConstrained = true
  MakeInternals = false
  MapMode = 5
  Placement = pos=(4e-15,4e-15,36) rot=(0,0,1;0rad)
  expr: Constraints[13] = 9
  sketch-geometry (5):
    g0: Circle [constr] CenterX=0 CenterY=0 CenterZ=0 NormalX=0 NormalY=0 NormalZ=1 AngleXU=0 Radius=52.0776
    g1: Circle CenterX=0 CenterY=0 CenterZ=0 NormalX=0 NormalY=0 NormalZ=1 AngleXU=0 Radius=42.5776
    g2: Circle CenterX=0 CenterY=0 CenterZ=0 NormalX=0 NormalY=0 NormalZ=1 AngleXU=0 Radius=51.5776
    g3: LineSegment [constr] StartX=-42.5776 StartY=0 StartZ=0 EndX=-42.0776 EndY=0 EndZ=0
    g4: LineSegment [constr] StartX=-52.0776 StartY=0 StartZ=0 EndX=-51.5776 EndY=0 EndZ=0
  constraints (14):
    c: Coincident(g0,g-3)
    c: PointOnObject(g-4,g0)
    c: Coincident(g1,g0)
    c: Coincident(g2,g0)
    c: PointOnObject(g3,g1)
    c: PointOnObject(g3,g-3)
    c: PointOnObject(g3,g-1)
    c: PointOnObject(g3,g-1)
    c: PointOnObject(g4,g0)
    c: PointOnObject(g4,g2)
    c: PointOnObject(g4,g-1)
    c: PointOnObject(g4,g-1)
    c: Equal(g4,g3)
    c: Distance(g2,g1) = 9
FEATURE [PartDesign::Pocket] Pocket005
  BaseFeature = -> PolarPattern
  Direction = (0,0,-1)
  Length = 3
  Length2 = 5
  Profile = -> Sketch015
  ReferenceAxis = -> Sketch015 [N_Axis]
  Refine = true
  SideType = 0
  Suppressed = false
  Type = 0
  Type2 = 0
  expr: Length = 3
FEATURE [PartDesign::Fillet] Fillet003
  Base = -> Pocket005 [Edge312,Edge949]
  BaseFeature = -> Pocket005
  Radius = 1
  Refine = true
  SupportTransform = false
  Suppressed = false
  UseAllEdges = false
  expr: Radius = 1
FEATURE [Sketcher::SketchObject] Sketch016
  ArcFitTolerance = 1e-06
  AttachmentSupport = -> [Fillet003]
  ExternalGeometry = -> [Fillet003]
  ExternalTypes = [0]
  FullyConstrained = false
  MakeInternals = false
  MapMode = 5
  Placement = pos=(0,0,33) rot=(0,0,1;0rad)
  sketch-geometry (8):
    g0: ArcOfCircle CenterX=4e-15 CenterY=4e-15 CenterZ=0 NormalX=0 NormalY=0 NormalZ=1 AngleXU=0 Radius=44.0776 StartAngle=1.01451 EndAngle=1.42895
    g1: ArcOfCircle CenterX=4e-15 CenterY=4e-15 CenterZ=0 NormalX=0 NormalY=0 NormalZ=1 AngleXU=0 Radius=50.0776 StartAngle=1.01451 EndAngle=1.42895
    g2: LineSegment StartX=6.23147 StartY=43.6349 StartZ=0 EndX=7.07972 EndY=49.5746 EndZ=0
    g3: LineSegment StartX=23.2744 StartY=37.4318 StartZ=0 EndX=26.4426 EndY=42.5271 EndZ=0
    g4: LineSegment [constr] StartX=23.2744 StartY=37.4318 StartZ=0 EndX=23.0104 EndY=37.0071 EndZ=0
    g5: LineSegment [constr] StartX=26.4426 StartY=42.5271 StartZ=0 EndX=26.7066 EndY=42.9517 EndZ=0
    g6: LineSegment [constr] StartX=4e-15 StartY=4e-15 StartZ=0 EndX=-40.9495 EndY=14.9044 EndZ=0
    g7: LineSegment [constr] StartX=4e-15 StartY=4e-15 StartZ=0 EndX=14.9044 EndY=40.9495 EndZ=0
  constraints (22):
    c: Coincident(g0,g-4)
    c: Coincident(g1,g0)
    c: Coincident(g2,g0)
    c: Coincident(g2,g1)
    c: Coincident(g3,g0)
    c: Coincident(g3,g1)
    c: Equal(g2,g3)
    c: Perpendicular(g0,g2)
    c: Coincident(g4,g0)
    c: PointOnObject(g4,g-4)
    c: Coincident(g5,g1)
    c: PointOnObject(g5,g-3)
    c: Parallel(g4,g3)
    c: Parallel(g3,g5)
    c: Equal(g5,g4)
    c: Distance(g3,g3) = 6
    c: Coincident(g6,g0)
    c: Angle(g6,g-1) = 0.349066
    c: PointOnObject(g6,g-4)
    c: Coincident(g7,g0)
    c: Perpendicular(g6,g7)
    c: Equal(g7,g6)
FEATURE [PartDesign::Pad] Pad004
  BaseFeature = -> Fillet003
  Direction = (0,0,1)
  Length = 1.5
  Length2 = 10
  Profile = -> Sketch016
  ReferenceAxis = -> Sketch016 [N_Axis]
  Refine = true
  SideType = 0
  Suppressed = false
  Type = 0
  Type2 = 0
  expr: Length = 1.5
FEATURE [PartDesign::PolarPattern] PolarPattern002
  Angle = 360
  Axis = -> Sketch016 [N_Axis]
  BaseFeature = -> Pad004
  Mode = 0
  Occurrences = 2
  Offset = 120
  Originals = -> [Pad004]
  Refine = true
  Suppressed = false
  TransformMode = 0
FEATURE [PartDesign::Fillet] Fillet004
  Base = -> PolarPattern002 [Face177,Face175]
  BaseFeature = -> PolarPattern002
  Radius = 1
  Refine = true
  SupportTransform = false
  Suppressed = false
  UseAllEdges = false
FEATURE [PartDesign::Body] Body016  label="outer_gear"
  AllowCompound = false
  Group = -> [InternalInvoluteGear,DatumPlane002,Sketch010,Revolution001,Sketch011,Revolution002,PolarPattern,Sketch015,Pocket005,Fillet003,Sketch016,Pad004,PolarPattern002,Fillet004]
  Origin = -> Origin026
  Placement = pos=(0,0,41) rot=(0,0,1;0rad)
  Tip = -> Fillet004
FEATURE [Measure::MeasureDistance] Distance  label="Distance: 93.99 mm"
  Distance = 93.9866
  DistanceX = 93.9866
  DistanceY = 1.42e-14
  DistanceZ = 0
  Element1 = -> Body016 [InternalInvoluteGear.Edge397]
  Element2 = -> Body016 [InternalInvoluteGear.Edge769]
  Position1 = (-46.9933,-3.16864,46)
  Position2 = (46.9933,-3.16864,46)
FEATURE [PartDesign::Pad] Pad005
  Direction = (0,0,1)
  Length = 3
  Length2 = 10
  Profile = -> Sketch012 [Edge2,Edge1]
  ReferenceAxis = -> Sketch012 [N_Axis]
  Refine = true
  SideType = 0
  Suppressed = false
  Type = 0
  Type2 = 0
  expr: Length = 3
FEATURE [Part::DatumPlane] DatumPlane003
  AttachmentSupport = -> [Sketch012]
  MapMode = 7
  Placement = pos=(40,0,0) rot=(1,0,0;1.5708rad)
FEATURE [Sketcher::SketchObject] Sketch017
  ArcFitTolerance = 1e-06
  AttachmentSupport = -> [DatumPlane003]
  ExternalTypes = [0]
  FullyConstrained = true
  MakeInternals = false
  MapMode = 5
  Placement = pos=(40,0,0) rot=(1,0,0;1.5708rad)
  expr: Constraints[4] = 14
  sketch-geometry (6):
    g0: LineSegment StartX=5.78797 StartY=-27 StartZ=0 EndX=5.78797 EndY=-13 EndZ=0
    g1: LineSegment StartX=5.78797 StartY=-13 StartZ=0 EndX=0 EndY=0 EndZ=0
    g2: LineSegment StartX=0 StartY=0 StartZ=0 EndX=-1.5 EndY=0 EndZ=0
    g3: LineSegment StartX=-1.5 StartY=0 StartZ=0 EndX=4.28797 EndY=-13 EndZ=0
    g4: LineSegment StartX=4.28797 StartY=-13 StartZ=0 EndX=4.28797 EndY=-27 EndZ=0
    g5: LineSegment StartX=4.28797 StartY=-27 StartZ=0 EndX=5.78797 EndY=-27 EndZ=0
  constraints (17):
    c: Vertical(g0)
    c: Coincident(g1,g0)
    c: Coincident(g1,g-1)
    c: Angle(g0,g1) = 0.418879
    c: DistanceY(g0,g0) = 14
    c: DistanceY(g0,g1) = 27
    c: Coincident(g2,g1)
    c: PointOnObject(g2,g-1)
    c: Coincident(g2,g3)
    c: Coincident(g3,g4)
    c: Vertical(g4)
    c: Coincident(g4,g5)
    c: Coincident(g5,g0)
    c: Perpendicular(g4,g5)
    c: Equal(g3,g1)
    c: Parallel(g3,g1)
    c: DistanceX(g5,g5) = 1.5
FEATURE [PartDesign::Revolution] Revolution003
  Angle = 360
  Angle2 = 60
  Axis = (1e-16,1e-16,1)
  Base = (0,0,0)
  BaseFeature = -> Pad005
  Profile = -> Sketch017
  ReferenceAxis = -> Z_Axis017
  Refine = true
  Reversed = true
  Suppressed = false
  Type = 0
FEATURE [PartDesign::Chamfer] Chamfer
  Angle = 45
  Base = -> Revolution003 [Edge13,Edge10]
  BaseFeature = -> Revolution003
  ChamferType = 0
  FlipDirection = false
  Refine = true
  Size = 2
  Size2 = 1
  SupportTransform = false
  Suppressed = false
  UseAllEdges = false
FEATURE [Part::DatumPlane] DatumPlane004
  AttachmentSupport = -> [Chamfer]
  MapMode = 7
  Placement = pos=(44.288,-6.1e-15,-27) rot=(0,0.707107,0.707107;3.14159rad)
FEATURE [Sketcher::SketchObject] Sketch018
  ArcFitTolerance = 1e-06
  AttachmentSupport = -> [DatumPlane004]
  ExternalTypes = [0]
  FullyConstrained = true
  MakeInternals = false
  MapMode = 5
  Placement = pos=(44.288,-6.1e-15,-27) rot=(0,0.707107,0.707107;3.14159rad)
  sketch-geometry (4):
    g0: LineSegment StartX=0 StartY=0 StartZ=0 EndX=0 EndY=5.12132 EndZ=0
    g1: LineSegment StartX=0 StartY=5.12132 StartZ=0 EndX=2.12132 EndY=3 EndZ=0
    g2: LineSegment StartX=2.12132 StartY=3 StartZ=0 EndX=2.12132 EndY=0 EndZ=0
    g3: LineSegment StartX=2.12132 StartY=0 StartZ=0 EndX=0 EndY=0 EndZ=0
  constraints (11):
    c: Coincident(g-1,g0)
    c: Vertical(g0)
    c: Coincident(g0,g1)
    c: Coincident(g1,g2)
    c: PointOnObject(g2,g-1)
    c: Vertical(g2)
    c: Coincident(g2,g3)
    c: Coincident(g3,g0)
    c: Angle(g2,g1) = 0.785398
    c: Equal(g2,g1)
    c: DistanceY(g2,g2) = 3
FEATURE [PartDesign::Revolution] Revolution004
  Angle = 9
  Angle2 = 60
  Axis = (1e-16,1e-16,1)
  Base = (0,0,0)
  BaseFeature = -> Chamfer
  Profile = -> Sketch018
  ReferenceAxis = -> Z_Axis017
  Refine = true
  Suppressed = false
  Type = 0
  expr: Angle = 9
FEATURE [PartDesign::PolarPattern] PolarPattern003
  Angle = 360
  Axis = -> Z_Axis017
  BaseFeature = -> Revolution004
  Mode = 0
  Occurrences = 4
  Offset = 120
  Originals = -> [Revolution004]
  Refine = true
  Suppressed = false
  TransformMode = 0
FEATURE [Sketcher::SketchObject] Sketch019
  ArcFitTolerance = 1e-06
  AttachmentSupport = -> [Fillet]
  ExternalTypes = [0]
  FullyConstrained = true
  MakeInternals = false
  MapMode = 5
  Placement = pos=(0,0,12) rot=(0,0,1;0rad)
  sketch-geometry (1):
    g0: Circle CenterX=0 CenterY=0 CenterZ=0 NormalX=0 NormalY=0 NormalZ=1 AngleXU=0 Radius=44
  constraints (2):
    c: Diameter(g0) = 88
    c: Coincident(g0,g-1)
FEATURE [Part::DatumPlane] DatumPlane005
  AttachmentSupport = -> [Sketch019]
  MapMode = 7
  Placement = pos=(44,0,12) rot=(1,0,0;1.5708rad)
FEATURE [Sketcher::SketchObject] Sketch020
  ArcFitTolerance = 1e-06
  AttachmentSupport = -> [DatumPlane005]
  ExternalTypes = [0]
  FullyConstrained = true
  MakeInternals = false
  MapMode = 5
  Placement = pos=(44,0,12) rot=(1,0,0;1.5708rad)
  sketch-geometry (9):
    g0: LineSegment StartX=-2.19203 StartY=0 StartZ=0 EndX=-2.19203 EndY=3.1 EndZ=0
    g1: LineSegment StartX=-2.19203 StartY=3.1 StartZ=0 EndX=0 EndY=5.29203 EndZ=0
    g2: LineSegment StartX=0 StartY=5.29203 StartZ=0 EndX=0 EndY=7.79203 EndZ=0
    g3: LineSegment StartX=-5.9535 StartY=0 StartZ=0 EndX=-2.19203 EndY=0 EndZ=0
    g4: LineSegment StartX=0 StartY=7.79203 StartZ=0 EndX=-3.44203 EndY=4.35 EndZ=0
    g5: LineSegment StartX=-3.44203 StartY=4.35 StartZ=0 EndX=-5.9535 EndY=0 EndZ=0
    g6: LineSegment [constr] StartX=-3.44203 StartY=4.35 StartZ=0 EndX=-2.19203 EndY=3.1 EndZ=0
    g7: LineSegment StartX=-2.19203 StartY=0 StartZ=0 EndX=0 EndY=0 EndZ=0
    g8: LineSegment StartX=0 StartY=0 StartZ=0 EndX=0 EndY=5.29203 EndZ=0
  constraints (24):
    c: PointOnObject(g0,g-1)
    c: Vertical(g0)
    c: Coincident(g0,g1)
    c: PointOnObject(g1,g-2)
    c: Coincident(g1,g2)
    c: Coincident(g3,g0)
    c: PointOnObject(g3,g-1)
    c: PointOnObject(g2,g-2)
    c: Angle(g1,g0) = 0.785398
    c: DistanceY(g0,g0) = 3.1
    c: Equal(g1,g0)
    c: DistanceY(g2,g2) = 2.5
    c: Coincident(g2,g4)
    c: Coincident(g4,g5)
    c: Coincident(g3,g5)
    c: Angle(g3,g5) = 1.0472
    c: Parallel(g4,g1)
    c: Coincident(g6,g4)
    c: Coincident(g6,g0)
    c: Perpendicular(g4,g6)
    c: Coincident(g7,g0)
    c: Coincident(g7,g-1)
    c: Coincident(g8,g7)
    c: Coincident(g8,g1)
FEATURE [PartDesign::Revolution] Revolution005
  Angle = 323
  Angle2 = 47
  Axis = (1e-16,1e-16,1)
  Base = (0,0,0)
  BaseFeature = -> Fillet
  Profile = -> Sketch020 [Edge4,Edge5,Edge2,Edge1,Edge3,Edge6]
  ReferenceAxis = -> Z_Axis003
  Refine = true
  Reversed = true
  Suppressed = false
  Type = 4
  expr: Angle = 323
  expr: Angle2 = 47
FEATURE [PartDesign::Revolution] Revolution006
  Angle = 313
  Angle2 = 53
  Axis = (1e-16,1e-16,1)
  Base = (0,0,0)
  BaseFeature = -> Revolution005
  Profile = -> Sketch020 [Edge8,Edge3,Edge4,Edge5,Edge6,Edge7]
  ReferenceAxis = -> Z_Axis003
  Refine = true
  Reversed = true
  Suppressed = false
  Type = 4
  expr: Angle = 313
  expr: Angle2 = 53
FEATURE [PartDesign::PolarPattern] PolarPattern004
  Angle = 360
  Axis = -> Z_Axis003
  BaseFeature = -> Revolution006
  Mode = 0
  Occurrences = 4
  Offset = 120
  Originals = -> [Revolution005,Revolution006]
  Refine = true
  Suppressed = false
  TransformMode = 0
  expr: Occurrences = 4
FEATURE [PartDesign::Fillet] Fillet005
  Base = -> PolarPattern004 [Face58,Face22]
  BaseFeature = -> PolarPattern004
  Radius = 0.5
  Refine = true
  SupportTransform = false
  Suppressed = false
  UseAllEdges = false
  expr: Radius = 0.5
FEATURE [PartDesign::Fillet] Fillet006
  Base = -> Fillet005 [Face21,Face18]
  BaseFeature = -> Fillet005
  Radius = 0.5
  Refine = true
  SupportTransform = false
  Suppressed = false
  UseAllEdges = false
  expr: Radius = 0.5
FEATURE [PartDesign::Fillet] Fillet007
  Base = -> Fillet006 [Face29,Face32]
  BaseFeature = -> Fillet006
  Radius = 0.5
  Refine = true
  SupportTransform = false
  Suppressed = false
  UseAllEdges = false
FEATURE [PartDesign::Fillet] Fillet008
  Base = -> Fillet007 [Face44,Face41]
  BaseFeature = -> Fillet007
  Radius = 0.5
  Refine = true
  SupportTransform = false
  Suppressed = false
  UseAllEdges = false
FEATURE [PartDesign::Body] Body003
  AllowCompound = false
  Group = -> [Sketch003,Pad,Sketch004,Pad001,Sketch005,Pocket001,Sketch006,Pocket002,Sketch007,Pocket003,DatumPlane001,Sketch009,Revolution,Fillet,Sketch019,DatumPlane005,Sketch020,Revolution005,Revolution006,PolarPattern004,Fillet005,Fillet006,Fillet007,Fillet008]
  Origin = -> Origin006
  Tip = -> Fillet008
FEATURE [Measure::MeasurePython] Center_of_mass  label="Center_of_mass: "  # WARN: FeaturePython — macro-defined, semantics opaque (R4)
  Element = -> Body003 [Pad001.Sketch004.]
  Placement = pos=(2.187e-13,6e-16,6) rot=(0,0,1;0rad)
  Result = (2.187e-13,6e-16,6)
FEATURE [PartDesign::Fillet] Fillet009
  Base = -> PolarPattern003 [Face21,Face22,Face23,Face7]
  BaseFeature = -> PolarPattern003
  Radius = 0.5
  Refine = true
  SupportTransform = false
  Suppressed = false
  UseAllEdges = false
  expr: Radius = 0.5
FEATURE [PartDesign::Body] Body021  label="upper_cover_display"
  AllowCompound = false
  Group = -> [Sketch012,Pad005,DatumPlane003,Sketch017,Revolution003,Chamfer,DatumPlane004,Sketch018,Revolution004,PolarPattern003,Fillet009]
  Origin = -> Origin034
  Tip = -> Fillet009
FEATURE [App::Point] Origin037
  Role = Origin
FEATURE [Sketcher::SketchObject] Sketch021
  ArcFitTolerance = 1e-06
  AttachmentSupport = -> [Origin036]
  ExternalTypes = [0]
  FullyConstrained = true
  MakeInternals = false
  MapMode = 5
  expr: Constraints[2] = 42.75 * 2
  expr: Constraints[3] = 51 * 2
  sketch-geometry (2):
    g0: Circle CenterX=0 CenterY=0 CenterZ=0 NormalX=0 NormalY=0 NormalZ=1 AngleXU=0 Radius=42.75
    g1: Circle CenterX=0 CenterY=0 CenterZ=0 NormalX=0 NormalY=0 NormalZ=1 AngleXU=0 Radius=51
  constraints (4):
    c: Coincident(g0,g-1)
    c: Coincident(g1,g0)
    c: Diameter(g0) = 85.5
    c: Diameter(g1) = 102
FEATURE [PartDesign::Pad] Pad006
  Direction = (0,0,1)
  Length = 3
  Length2 = 10
  Profile = -> Sketch021
  ReferenceAxis = -> Sketch021 [N_Axis]
  Refine = true
  SideType = 0
  Suppressed = false
  Type = 0
  Type2 = 0
  expr: Length = 3
FEATURE [Sketcher::SketchObject] Sketch022
  ArcFitTolerance = 1e-06
  AttachmentSupport = -> [Pad006]
  ExternalTypes = [0]
  FullyConstrained = false
  MakeInternals = false
  MapMode = 5
  Placement = pos=(0,0,3) rot=(0,0,1;0rad)
  sketch-geometry (4):
    g0: ArcOfCircle CenterX=0 CenterY=0 CenterZ=0 NormalX=0 NormalY=0 NormalZ=1 AngleXU=0 Radius=44.0776 StartAngle=1.01451 EndAngle=1.42895
    g1: ArcOfCircle CenterX=0 CenterY=0 CenterZ=0 NormalX=0 NormalY=0 NormalZ=1 AngleXU=0 Radius=50.0776 StartAngle=1.01451 EndAngle=1.42895
    g2: LineSegment StartX=6.23147 StartY=43.6349 StartZ=0 EndX=7.07972 EndY=49.5746 EndZ=0
    g3: LineSegment StartX=23.2744 StartY=37.4317 StartZ=0 EndX=26.4426 EndY=42.5271 EndZ=0
  constraints (8):
    c: Coincident(g1,g0)
    c: Coincident(g2,g0)
    c: Coincident(g2,g1)
    c: Coincident(g3,g0)
    c: Coincident(g3,g1)
    c: Equal(g2,g3)
    c: Perpendicular(g0,g2)
    c: Distance(g3,g3) = 6
FEATURE [PartDesign::Pocket] Pocket006
  BaseFeature = -> Pad006
  Direction = (0,0,-1)
  Length = 1.5
  Length2 = 5
  Profile = -> Sketch022
  ReferenceAxis = -> Sketch022 [N_Axis]
  Refine = true
  SideType = 0
  Suppressed = false
  Type = 0
  Type2 = 0
  expr: Length = 1.5
FEATURE [PartDesign::PolarPattern] PolarPattern005
  Angle = 360
  Axis = -> Sketch022 [N_Axis]
  BaseFeature = -> Pocket006
  Mode = 0
  Occurrences = 2
  Offset = 120
  Originals = -> [Pocket006]
  Refine = true
  Suppressed = false
  TransformMode = 0
FEATURE [PartDesign::Fillet] Fillet010
  Base = -> PolarPattern005 [Face2]
  BaseFeature = -> PolarPattern005
  Radius = 0.3
  Refine = true
  SupportTransform = false
  Suppressed = false
  UseAllEdges = false
  expr: Radius = 0.3
FEATURE [PartDesign::Fillet] Fillet011
  Base = -> Fillet010 [Face3]
  BaseFeature = -> Fillet010
  Radius = 0.4
  Refine = true
  SupportTransform = false
  Suppressed = false
  UseAllEdges = false
  expr: Radius = 0.4
FEATURE [Sketcher::SketchObject] Sketch023
  ArcFitTolerance = 1e-06
  AttachmentSupport = -> [Fillet011]
  ExternalTypes = [0]
  FullyConstrained = false
  MakeInternals = false
  MapMode = 5
  Placement = pos=(0,0,0) rot=(1,0,0;3.14159rad)
  sketch-geometry (1190):
    g0: BSplineCurve PolesCount=2 KnotsCount=2 Degree=1 IsPeriodic=0
    g1: BSplineCurve PolesCount=2 KnotsCount=2 Degree=1 IsPeriodic=0
    g2: BSplineCurve PolesCount=2 KnotsCount=2 Degree=1 IsPeriodic=0
    g3: BSplineCurve PolesCount=2 KnotsCount=2 Degree=1 IsPeriodic=0
    g4: BSplineCurve PolesCount=2 KnotsCount=2 Degree=1 IsPeriodic=0
    g5: BSplineCurve PolesCount=2 KnotsCount=2 Degree=1 IsPeriodic=0
    g6: BSplineCurve PolesCount=2 KnotsCount=2 Degree=1 IsPeriodic=0
    g7: BSplineCurve PolesCount=2 KnotsCount=2 Degree=1 IsPeriodic=0
    g8: BSplineCurve PolesCount=2 KnotsCount=2 Degree=1 IsPeriodic=0
    g9: BSplineCurve PolesCount=2 KnotsCount=2 Degree=1 IsPeriodic=0
    g10: BSplineCurve PolesCount=2 KnotsCount=2 Degree=1 IsPeriodic=0
    g11: BSplineCurve PolesCount=2 KnotsCount=2 Degree=1 IsPeriodic=0
    g12: BSplineCurve PolesCount=2 KnotsCount=2 Degree=1 IsPeriodic=0
    g13: BSplineCurve PolesCount=2 KnotsCount=2 Degree=1 IsPeriodic=0
    g14: BSplineCurve PolesCount=2 KnotsCount=2 Degree=1 IsPeriodic=0
    g15: BSplineCurve PolesCount=2 KnotsCount=2 Degree=1 IsPeriodic=0
    g16: BSplineCurve PolesCount=2 KnotsCount=2 Degree=1 IsPeriodic=0
    g17: BSplineCurve PolesCount=2 KnotsCount=2 Degree=1 IsPeriodic=0
    g18: BSplineCurve PolesCount=2 KnotsCount=2 Degree=1 IsPeriodic=0
    g19: BSplineCurve PolesCount=2 KnotsCount=2 Degree=1 IsPeriodic=0
    g20: BSplineCurve PolesCount=2 KnotsCount=2 Degree=1 IsPeriodic=0
    g21: BSplineCurve PolesCount=2 KnotsCount=2 Degree=1 IsPeriodic=0
    g22: BSplineCurve PolesCount=2 KnotsCount=2 Degree=1 IsPeriodic=0
    g23: BSplineCurve PolesCount=2 KnotsCount=2 Degree=1 IsPeriodic=0
    g24: BSplineCurve PolesCount=2 KnotsCount=2 Degree=1 IsPeriodic=0
    g25: BSplineCurve PolesCount=2 KnotsCount=2 Degree=1 IsPeriodic=0
    g26: BSplineCurve PolesCount=2 KnotsCount=2 Degree=1 IsPeriodic=0
    g27: BSplineCurve PolesCount=2 KnotsCount=2 Degree=1 IsPeriodic=0
    g28: BSplineCurve PolesCount=2 KnotsCount=2 Degree=1 IsPeriodic=0
    g29: BSplineCurve PolesCount=2 KnotsCount=2 Degree=1 IsPeriodic=0
    g30: BSplineCurve PolesCount=2 KnotsCount=2 Degree=1 IsPeriodic=0
    g31: BSplineCurve PolesCount=2 KnotsCount=2 Degree=1 IsPeriodic=0
    g32: BSplineCurve PolesCount=2 KnotsCount=2 Degree=1 IsPeriodic=0
    g33: BSplineCurve PolesCount=2 KnotsCount=2 Degree=1 IsPeriodic=0
    g34: BSplineCurve PolesCount=2 KnotsCount=2 Degree=1 IsPeriodic=0
    g35: BSplineCurve PolesCount=2 KnotsCount=2 Degree=1 IsPeriodic=0
    g36: BSplineCurve PolesCount=2 KnotsCount=2 Degree=1 IsPeriodic=0
    g37: BSplineCurve PolesCount=2 KnotsCount=2 Degree=1 IsPeriodic=0
    g38: BSplineCurve PolesCount=2 KnotsCount=2 Degree=1 IsPeriodic=0
    g39: BSplineCurve PolesCount=2 KnotsCount=2 Degree=1 IsPeriodic=0
    g40: BSplineCurve PolesCount=2 KnotsCount=2 Degree=1 IsPeriodic=0
    g41: BSplineCurve PolesCount=2 KnotsCount=2 Degree=1 IsPeriodic=0
    g42: BSplineCurve PolesCount=2 KnotsCount=2 Degree=1 IsPeriodic=0
    g43: BSplineCurve PolesCount=2 KnotsCount=2 Degree=1 IsPeriodic=0
    g44: BSplineCurve PolesCount=2 KnotsCount=2 Degree=1 IsPeriodic=0
    g45: BSplineCurve PolesCount=2 KnotsCount=2 Degree=1 IsPeriodic=0
    g46: BSplineCurve PolesCount=2 KnotsCount=2 Degree=1 IsPeriodic=0
    g47: BSplineCurve PolesCount=2 KnotsCount=2 Degree=1 IsPeriodic=0
    g48: BSplineCurve PolesCount=2 KnotsCount=2 Degree=1 IsPeriodic=0
    g49: BSplineCurve PolesCount=2 KnotsCount=2 Degree=1 IsPeriodic=0
    g50: BSplineCurve PolesCount=2 KnotsCount=2 Degree=1 IsPeriodic=0
    g51: BSplineCurve PolesCount=2 KnotsCount=2 Degree=1 IsPeriodic=0
    g52: BSplineCurve PolesCount=2 KnotsCount=2 Degree=1 IsPeriodic=0
    g53: BSplineCurve PolesCount=2 KnotsCount=2 Degree=1 IsPeriodic=0
    g54: BSplineCurve PolesCount=2 KnotsCount=2 Degree=1 IsPeriodic=0
    g55: BSplineCurve PolesCount=2 KnotsCount=2 Degree=1 IsPeriodic=0
    g56: BSplineCurve PolesCount=2 KnotsCount=2 Degree=1 IsPeriodic=0
    g57: BSplineCurve PolesCount=2 KnotsCount=2 Degree=1 IsPeriodic=0
    g58: BSplineCurve PolesCount=2 KnotsCount=2 Degree=1 IsPeriodic=0
    g59: BSplineCurve PolesCount=2 KnotsCount=2 Degree=1 IsPeriodic=0
    g60: BSplineCurve PolesCount=2 KnotsCount=2 Degree=1 IsPeriodic=0
    g61: BSplineCurve PolesCount=2 KnotsCount=2 Degree=1 IsPeriodic=0
    g62: BSplineCurve PolesCount=2 KnotsCount=2 Degree=1 IsPeriodic=0
    g63: BSplineCurve PolesCount=2 KnotsCount=2 Degree=1 IsPeriodic=0
    g64: BSplineCurve PolesCount=2 KnotsCount=2 Degree=1 IsPeriodic=0
    g65: BSplineCurve PolesCount=2 KnotsCount=2 Degree=1 IsPeriodic=0
    g66: BSplineCurve PolesCount=2 KnotsCount=2 Degree=1 IsPeriodic=0
    g67: BSplineCurve PolesCount=2 KnotsCount=2 Degree=1 IsPeriodic=0
    g68: BSplineCurve PolesCount=2 KnotsCount=2 Degree=1 IsPeriodic=0
    g69: BSplineCurve PolesCount=2 KnotsCount=2 Degree=1 IsPeriodic=0
    g70: BSplineCurve PolesCount=2 KnotsCount=2 Degree=1 IsPeriodic=0
    g71: BSplineCurve PolesCount=2 KnotsCount=2 Degree=1 IsPeriodic=0
    g72: BSplineCurve PolesCount=2 KnotsCount=2 Degree=1 IsPeriodic=0
    g73: BSplineCurve PolesCount=2 KnotsCount=2 Degree=1 IsPeriodic=0
    g74: BSplineCurve PolesCount=2 KnotsCount=2 Degree=1 IsPeriodic=0
    g75: BSplineCurve PolesCount=2 KnotsCount=2 Degree=1 IsPeriodic=0
    g76: BSplineCurve PolesCount=2 KnotsCount=2 Degree=1 IsPeriodic=0
    g77: BSplineCurve PolesCount=2 KnotsCount=2 Degree=1 IsPeriodic=0
    g78: BSplineCurve PolesCount=2 KnotsCount=2 Degree=1 IsPeriodic=0
    g79: BSplineCurve PolesCount=2 KnotsCount=2 Degree=1 IsPeriodic=0
    g80: BSplineCurve PolesCount=2 KnotsCount=2 Degree=1 IsPeriodic=0
    g81: BSplineCurve PolesCount=2 KnotsCount=2 Degree=1 IsPeriodic=0
    g82: BSplineCurve PolesCount=2 KnotsCount=2 Degree=1 IsPeriodic=0
    g83: BSplineCurve PolesCount=2 KnotsCount=2 Degree=1 IsPeriodic=0
    g84: BSplineCurve PolesCount=2 KnotsCount=2 Degree=1 IsPeriodic=0
    g85: BSplineCurve PolesCount=2 KnotsCount=2 Degree=1 IsPeriodic=0
    g86: BSplineCurve PolesCount=2 KnotsCount=2 Degree=1 IsPeriodic=0
    g87: BSplineCurve PolesCount=2 KnotsCount=2 Degree=1 IsPeriodic=0
    g88: BSplineCurve PolesCount=2 KnotsCount=2 Degree=1 IsPeriodic=0
    g89: BSplineCurve PolesCount=2 KnotsCount=2 Degree=1 IsPeriodic=0
    g90: BSplineCurve PolesCount=2 KnotsCount=2 Degree=1 IsPeriodic=0
    g91: BSplineCurve PolesCount=2 KnotsCount=2 Degree=1 IsPeriodic=0
    g92: BSplineCurve PolesCount=2 KnotsCount=2 Degree=1 IsPeriodic=0
    g93: BSplineCurve PolesCount=2 KnotsCount=2 Degree=1 IsPeriodic=0
    g94: BSplineCurve PolesCount=2 KnotsCount=2 Degree=1 IsPeriodic=0
    g95: BSplineCurve PolesCount=2 KnotsCount=2 Degree=1 IsPeriodic=0
    g96: BSplineCurve PolesCount=2 KnotsCount=2 Degree=1 IsPeriodic=0
    g97: BSplineCurve PolesCount=2 KnotsCount=2 Degree=1 IsPeriodic=0
    g98: BSplineCurve PolesCount=2 KnotsCount=2 Degree=1 IsPeriodic=0
    g99: BSplineCurve PolesCount=2 KnotsCount=2 Degree=1 IsPeriodic=0
    g100: BSplineCurve PolesCount=2 KnotsCount=2 Degree=1 IsPeriodic=0
    g101: BSplineCurve PolesCount=2 KnotsCount=2 Degree=1 IsPeriodic=0
    g102: BSplineCurve PolesCount=2 KnotsCount=2 Degree=1 IsPeriodic=0
    g103: BSplineCurve PolesCount=2 KnotsCount=2 Degree=1 IsPeriodic=0
    g104: BSplineCurve PolesCount=2 KnotsCount=2 Degree=1 IsPeriodic=0
    g105: BSplineCurve PolesCount=2 KnotsCount=2 Degree=1 IsPeriodic=0
    g106: BSplineCurve PolesCount=2 KnotsCount=2 Degree=1 IsPeriodic=0
    g107: BSplineCurve PolesCount=2 KnotsCount=2 Degree=1 IsPeriodic=0
    g108: BSplineCurve PolesCount=2 KnotsCount=2 Degree=1 IsPeriodic=0
    g109: BSplineCurve PolesCount=2 KnotsCount=2 Degree=1 IsPeriodic=0
    g110: BSplineCurve PolesCount=2 KnotsCount=2 Degree=1 IsPeriodic=0
    g111: BSplineCurve PolesCount=2 KnotsCount=2 Degree=1 IsPeriodic=0
    g112: BSplineCurve PolesCount=2 KnotsCount=2 Degree=1 IsPeriodic=0
    g113: BSplineCurve PolesCount=2 KnotsCount=2 Degree=1 IsPeriodic=0
    g114: BSplineCurve PolesCount=2 KnotsCount=2 Degree=1 IsPeriodic=0
    g115: BSplineCurve PolesCount=2 KnotsCount=2 Degree=1 IsPeriodic=0
    g116: BSplineCurve PolesCount=2 KnotsCount=2 Degree=1 IsPeriodic=0
    g117: BSplineCurve PolesCount=2 KnotsCount=2 Degree=1 IsPeriodic=0
    g118: BSplineCurve PolesCount=2 KnotsCount=2 Degree=1 IsPeriodic=0
    g119: BSplineCurve PolesCount=2 KnotsCount=2 Degree=1 IsPeriodic=0
    g120: BSplineCurve PolesCount=2 KnotsCount=2 Degree=1 IsPeriodic=0
    g121: BSplineCurve PolesCount=2 KnotsCount=2 Degree=1 IsPeriodic=0
    g122: BSplineCurve PolesCount=2 KnotsCount=2 Degree=1 IsPeriodic=0
    g123: BSplineCurve PolesCount=2 KnotsCount=2 Degree=1 IsPeriodic=0
    g124: BSplineCurve PolesCount=2 KnotsCount=2 Degree=1 IsPeriodic=0
    g125: BSplineCurve PolesCount=2 KnotsCount=2 Degree=1 IsPeriodic=0
    g126: BSplineCurve PolesCount=2 KnotsCount=2 Degree=1 IsPeriodic=0
    g127: BSplineCurve PolesCount=2 KnotsCount=2 Degree=1 IsPeriodic=0
    g128: BSplineCurve PolesCount=3 KnotsCount=2 Degree=2 IsPeriodic=0
    g129: BSplineCurve PolesCount=3 KnotsCount=2 Degree=2 IsPeriodic=0
    g130: BSplineCurve PolesCount=3 KnotsCount=2 Degree=2 IsPeriodic=0
    g131: BSplineCurve PolesCount=3 KnotsCount=2 Degree=2 IsPeriodic=0
    g132: BSplineCurve PolesCount=3 KnotsCount=2 Degree=2 IsPeriodic=0
    g133: BSplineCurve PolesCount=3 KnotsCount=2 Degree=2 IsPeriodic=0
    g134: BSplineCurve PolesCount=3 KnotsCount=2 Degree=2 IsPeriodic=0
    g135: BSplineCurve PolesCount=3 KnotsCount=2 Degree=2 IsPeriodic=0
    g136: BSplineCurve PolesCount=3 KnotsCount=2 Degree=2 IsPeriodic=0
    g137: BSplineCurve PolesCount=3 KnotsCount=2 Degree=2 IsPeriodic=0
    g138: BSplineCurve PolesCount=3 KnotsCount=2 Degree=2 IsPeriodic=0
    g139: BSplineCurve PolesCount=3 KnotsCount=2 Degree=2 IsPeriodic=0
    g140: BSplineCurve PolesCount=3 KnotsCount=2 Degree=2 IsPeriodic=0
    g141: BSplineCurve PolesCount=3 KnotsCount=2 Degree=2 IsPeriodic=0
    g142: BSplineCurve PolesCount=3 KnotsCount=2 Degree=2 IsPeriodic=0
    g143: BSplineCurve PolesCount=3 KnotsCount=2 Degree=2 IsPeriodic=0
    g144: BSplineCurve PolesCount=2 KnotsCount=2 Degree=1 IsPeriodic=0
    g145: BSplineCurve PolesCount=2 KnotsCount=2 Degree=1 IsPeriodic=0
    g146: BSplineCurve PolesCount=2 KnotsCount=2 Degree=1 IsPeriodic=0
    g147: BSplineCurve PolesCount=2 KnotsCount=2 Degree=1 IsPeriodic=0
    g148: BSplineCurve PolesCount=2 KnotsCount=2 Degree=1 IsPeriodic=0
    g149: BSplineCurve PolesCount=2 KnotsCount=2 Degree=1 IsPeriodic=0
    g150: BSplineCurve PolesCount=2 KnotsCount=2 Degree=1 IsPeriodic=0
    g151: BSplineCurve PolesCount=2 KnotsCount=2 Degree=1 IsPeriodic=0
    g152: BSplineCurve PolesCount=2 KnotsCount=2 Degree=1 IsPeriodic=0
    g153: BSplineCurve PolesCount=2 KnotsCount=2 Degree=1 IsPeriodic=0
    g154: BSplineCurve PolesCount=2 KnotsCount=2 Degree=1 IsPeriodic=0
    g155: BSplineCurve PolesCount=2 KnotsCount=2 Degree=1 IsPeriodic=0
    g156: BSplineCurve PolesCount=3 KnotsCount=2 Degree=2 IsPeriodic=0
    g157: BSplineCurve PolesCount=3 KnotsCount=2 Degree=2 IsPeriodic=0
    g158: BSplineCurve PolesCount=3 KnotsCount=2 Degree=2 IsPeriodic=0
    g159: BSplineCurve PolesCount=3 KnotsCount=2 Degree=2 IsPeriodic=0
    g160: BSplineCurve PolesCount=3 KnotsCount=2 Degree=2 IsPeriodic=0
    g161: BSplineCurve PolesCount=3 KnotsCount=2 Degree=2 IsPeriodic=0
    g162: BSplineCurve PolesCount=3 KnotsCount=2 Degree=2 IsPeriodic=0
    g163: BSplineCurve PolesCount=3 KnotsCount=2 Degree=2 IsPeriodic=0
    g164: BSplineCurve PolesCount=3 KnotsCount=2 Degree=2 IsPeriodic=0
    g165: BSplineCurve PolesCount=3 KnotsCount=2 Degree=2 IsPeriodic=0
    g166: BSplineCurve PolesCount=2 KnotsCount=2 Degree=1 IsPeriodic=0
    g167: BSplineCurve PolesCount=3 KnotsCount=2 Degree=2 IsPeriodic=0
    g168: BSplineCurve PolesCount=3 KnotsCount=2 Degree=2 IsPeriodic=0
    g169: BSplineCurve PolesCount=3 KnotsCount=2 Degree=2 IsPeriodic=0
    g170: BSplineCurve PolesCount=3 KnotsCount=2 Degree=2 IsPeriodic=0
    g171: BSplineCurve PolesCount=3 KnotsCount=2 Degree=2 IsPeriodic=0
    g172: BSplineCurve PolesCount=3 KnotsCount=2 Degree=2 IsPeriodic=0
    g173: BSplineCurve PolesCount=3 KnotsCount=2 Degree=2 IsPeriodic=0
    g174: BSplineCurve PolesCount=3 KnotsCount=2 Degree=2 IsPeriodic=0
    g175: BSplineCurve PolesCount=3 KnotsCount=2 Degree=2 IsPeriodic=0
    g176: BSplineCurve PolesCount=2 KnotsCount=2 Degree=1 IsPeriodic=0
    g177: BSplineCurve PolesCount=2 KnotsCount=2 Degree=1 IsPeriodic=0
    g178: BSplineCurve PolesCount=2 KnotsCount=2 Degree=1 IsPeriodic=0
    g179: BSplineCurve PolesCount=3 KnotsCount=2 Degree=2 IsPeriodic=0
    g180: BSplineCurve PolesCount=3 KnotsCount=2 Degree=2 IsPeriodic=0
    g181: BSplineCurve PolesCount=3 KnotsCount=2 Degree=2 IsPeriodic=0
    g182: BSplineCurve PolesCount=3 KnotsCount=2 Degree=2 IsPeriodic=0
    g183: BSplineCurve PolesCount=2 KnotsCount=2 Degree=1 IsPeriodic=0
    g184: BSplineCurve PolesCount=3 KnotsCount=2 Degree=2 IsPeriodic=0
    g185: BSplineCurve PolesCount=3 KnotsCount=2 Degree=2 IsPeriodic=0
    g186: BSplineCurve PolesCount=3 KnotsCount=2 Degree=2 IsPeriodic=0
    g187: BSplineCurve PolesCount=3 KnotsCount=2 Degree=2 IsPeriodic=0
    g188: BSplineCurve PolesCount=3 KnotsCount=2 Degree=2 IsPeriodic=0
    g189: BSplineCurve PolesCount=2 KnotsCount=2 Degree=1 IsPeriodic=0
    g190: BSplineCurve PolesCount=2 KnotsCount=2 Degree=1 IsPeriodic=0
    g191: BSplineCurve PolesCount=2 KnotsCount=2 Degree=1 IsPeriodic=0
    g192: BSplineCurve PolesCount=3 KnotsCount=2 Degree=2 IsPeriodic=0
    g193: BSplineCurve PolesCount=3 KnotsCount=2 Degree=2 IsPeriodic=0
    g194: BSplineCurve PolesCount=3 KnotsCount=2 Degree=2 IsPeriodic=0
    g195: BSplineCurve PolesCount=3 KnotsCount=2 Degree=2 IsPeriodic=0
    g196: BSplineCurve PolesCount=3 KnotsCount=2 Degree=2 IsPeriodic=0
    g197: BSplineCurve PolesCount=3 KnotsCount=2 Degree=2 IsPeriodic=0
    g198: BSplineCurve PolesCount=2 KnotsCount=2 Degree=1 IsPeriodic=0
    g199: BSplineCurve PolesCount=3 KnotsCount=2 Degree=2 IsPeriodic=0
    g200: BSplineCurve PolesCount=3 KnotsCount=2 Degree=2 IsPeriodic=0
    g201: BSplineCurve PolesCount=3 KnotsCount=2 Degree=2 IsPeriodic=0
    g202: BSplineCurve PolesCount=3 KnotsCount=2 Degree=2 IsPeriodic=0
    g203: BSplineCurve PolesCount=3 KnotsCount=2 Degree=2 IsPeriodic=0
    g204: BSplineCurve PolesCount=3 KnotsCount=2 Degree=2 IsPeriodic=0
    g205: BSplineCurve PolesCount=2 KnotsCount=2 Degree=1 IsPeriodic=0
    g206: BSplineCurve PolesCount=3 KnotsCount=2 Degree=2 IsPeriodic=0
    g207: BSplineCurve PolesCount=3 KnotsCount=2 Degree=2 IsPeriodic=0
    g208: BSplineCurve PolesCount=2 KnotsCount=2 Degree=1 IsPeriodic=0
    g209: BSplineCurve PolesCount=2 KnotsCount=2 Degree=1 IsPeriodic=0
    g210: BSplineCurve PolesCount=2 KnotsCount=2 Degree=1 IsPeriodic=0
    g211: BSplineCurve PolesCount=2 KnotsCount=2 Degree=1 IsPeriodic=0
    g212: BSplineCurve PolesCount=2 KnotsCount=2 Degree=1 IsPeriodic=0
    g213: BSplineCurve PolesCount=2 KnotsCount=2 Degree=1 IsPeriodic=0
    g214: BSplineCurve PolesCount=2 KnotsCount=2 Degree=1 IsPeriodic=0
    g215: BSplineCurve PolesCount=2 KnotsCount=2 Degree=1 IsPeriodic=0
    g216: BSplineCurve PolesCount=2 KnotsCount=2 Degree=1 IsPeriodic=0
    g217: BSplineCurve PolesCount=2 KnotsCount=2 Degree=1 IsPeriodic=0
    g218: BSplineCurve PolesCount=2 KnotsCount=2 Degree=1 IsPeriodic=0
    g219: BSplineCurve PolesCount=2 KnotsCount=2 Degree=1 IsPeriodic=0
    g220: BSplineCurve PolesCount=2 KnotsCount=2 Degree=1 IsPeriodic=0
    g221: BSplineCurve PolesCount=2 KnotsCount=2 Degree=1 IsPeriodic=0
    g222: BSplineCurve PolesCount=2 KnotsCount=2 Degree=1 IsPeriodic=0
    g223: BSplineCurve PolesCount=2 KnotsCount=2 Degree=1 IsPeriodic=0
    g224: BSplineCurve PolesCount=3 KnotsCount=2 Degree=2 IsPeriodic=0
    g225: BSplineCurve PolesCount=3 KnotsCount=2 Degree=2 IsPeriodic=0
    g226: BSplineCurve PolesCount=3 KnotsCount=2 Degree=2 IsPeriodic=0
    g227: BSplineCurve PolesCount=3 KnotsCount=2 Degree=2 IsPeriodic=0
    g228: BSplineCurve PolesCount=3 KnotsCount=2 Degree=2 IsPeriodic=0
    g229: BSplineCurve PolesCount=3 KnotsCount=2 Degree=2 IsPeriodic=0
    g230: BSplineCurve PolesCount=2 KnotsCount=2 Degree=1 IsPeriodic=0
    g231: BSplineCurve PolesCount=3 KnotsCount=2 Degree=2 IsPeriodic=0
    g232: BSplineCurve PolesCount=3 KnotsCount=2 Degree=2 IsPeriodic=0
    g233: BSplineCurve PolesCount=3 KnotsCount=2 Degree=2 IsPeriodic=0
    g234: BSplineCurve PolesCount=3 KnotsCount=2 Degree=2 IsPeriodic=0
    g235: BSplineCurve PolesCount=3 KnotsCount=2 Degree=2 IsPeriodic=0
    g236: BSplineCurve PolesCount=3 KnotsCount=2 Degree=2 IsPeriodic=0
    g237: BSplineCurve PolesCount=3 KnotsCount=2 Degree=2 IsPeriodic=0
    g238: BSplineCurve PolesCount=2 KnotsCount=2 Degree=1 IsPeriodic=0
    g239: BSplineCurve PolesCount=2 KnotsCount=2 Degree=1 IsPeriodic=0
    g240: BSplineCurve PolesCount=2 KnotsCount=2 Degree=1 IsPeriodic=0
    g241: BSplineCurve PolesCount=2 KnotsCount=2 Degree=1 IsPeriodic=0
    g242: BSplineCurve PolesCount=2 KnotsCount=2 Degree=1 IsPeriodic=0
    g243: BSplineCurve PolesCount=2 KnotsCount=2 Degree=1 IsPeriodic=0
    g244: BSplineCurve PolesCount=3 KnotsCount=2 Degree=2 IsPeriodic=0
    g245: BSplineCurve PolesCount=3 KnotsCount=2 Degree=2 IsPeriodic=0
    g246: BSplineCurve PolesCount=3 KnotsCount=2 Degree=2 IsPeriodic=0
    g247: BSplineCurve PolesCount=3 KnotsCount=2 Degree=2 IsPeriodic=0
    g248: BSplineCurve PolesCount=3 KnotsCount=2 Degree=2 IsPeriodic=0
    g249: BSplineCurve PolesCount=3 KnotsCount=2 Degree=2 IsPeriodic=0
    g250: BSplineCurve PolesCount=3 KnotsCount=2 Degree=2 IsPeriodic=0
    g251: BSplineCurve PolesCount=3 KnotsCount=2 Degree=2 IsPeriodic=0
    g252: BSplineCurve PolesCount=3 KnotsCount=2 Degree=2 IsPeriodic=0
    g253: BSplineCurve PolesCount=3 KnotsCount=2 Degree=2 IsPeriodic=0
    g254: BSplineCurve PolesCount=3 KnotsCount=2 Degree=2 IsPeriodic=0
    g255: BSplineCurve PolesCount=3 KnotsCount=2 Degree=2 IsPeriodic=0
    g256: BSplineCurve PolesCount=3 KnotsCount=2 Degree=2 IsPeriodic=0
    g257: BSplineCurve PolesCount=3 KnotsCount=2 Degree=2 IsPeriodic=0
    g258: BSplineCurve PolesCount=3 KnotsCount=2 Degree=2 IsPeriodic=0
    g259: BSplineCurve PolesCount=3 KnotsCount=2 Degree=2 IsPeriodic=0
    g260: BSplineCurve PolesCount=3 KnotsCount=2 Degree=2 IsPeriodic=0
    g261: BSplineCurve PolesCount=2 KnotsCount=2 Degree=1 IsPeriodic=0
    g262: BSplineCurve PolesCount=3 KnotsCount=2 Degree=2 IsPeriodic=0
    g263: BSplineCurve PolesCount=3 KnotsCount=2 Degree=2 IsPeriodic=0
    g264: BSplineCurve PolesCount=3 KnotsCount=2 Degree=2 IsPeriodic=0
    g265: BSplineCurve PolesCount=3 KnotsCount=2 Degree=2 IsPeriodic=0
    g266: BSplineCurve PolesCount=3 KnotsCount=2 Degree=2 IsPeriodic=0
    g267: BSplineCurve PolesCount=3 KnotsCount=2 Degree=2 IsPeriodic=0
    g268: BSplineCurve PolesCount=3 KnotsCount=2 Degree=2 IsPeriodic=0
    g269: BSplineCurve PolesCount=3 KnotsCount=2 Degree=2 IsPeriodic=0
    g270: BSplineCurve PolesCount=3 KnotsCount=2 Degree=2 IsPeriodic=0
    g271: BSplineCurve PolesCount=3 KnotsCount=2 Degree=2 IsPeriodic=0
    g272: BSplineCurve PolesCount=3 KnotsCount=2 Degree=2 IsPeriodic=0
    g273: BSplineCurve PolesCount=2 KnotsCount=2 Degree=1 IsPeriodic=0
    g274: BSplineCurve PolesCount=3 KnotsCount=2 Degree=2 IsPeriodic=0
    g275: BSplineCurve PolesCount=3 KnotsCount=2 Degree=2 IsPeriodic=0
    g276: BSplineCurve PolesCount=2 KnotsCount=2 Degree=1 IsPeriodic=0
    g277: BSplineCurve PolesCount=2 KnotsCount=2 Degree=1 IsPeriodic=0
    g278: BSplineCurve PolesCount=2 KnotsCount=2 Degree=1 IsPeriodic=0
    g279: BSplineCurve PolesCount=2 KnotsCount=2 Degree=1 IsPeriodic=0
    g280: BSplineCurve PolesCount=3 KnotsCount=2 Degree=2 IsPeriodic=0
    g281: BSplineCurve PolesCount=3 KnotsCount=2 Degree=2 IsPeriodic=0
    g282: BSplineCurve PolesCount=3 KnotsCount=2 Degree=2 IsPeriodic=0
    g283: BSplineCurve PolesCount=3 KnotsCount=2 Degree=2 IsPeriodic=0
    g284: BSplineCurve PolesCount=3 KnotsCount=2 Degree=2 IsPeriodic=0
    g285: BSplineCurve PolesCount=2 KnotsCount=2 Degree=1 IsPeriodic=0
    g286: BSplineCurve PolesCount=3 KnotsCount=2 Degree=2 IsPeriodic=0
    g287: BSplineCurve PolesCount=3 KnotsCount=2 Degree=2 IsPeriodic=0
    g288: BSplineCurve PolesCount=3 KnotsCount=2 Degree=2 IsPeriodic=0
    g289: BSplineCurve PolesCount=3 KnotsCount=2 Degree=2 IsPeriodic=0
    g290: BSplineCurve PolesCount=3 KnotsCount=2 Degree=2 IsPeriodic=0
    g291: BSplineCurve PolesCount=3 KnotsCount=2 Degree=2 IsPeriodic=0
    g292: BSplineCurve PolesCount=2 KnotsCount=2 Degree=1 IsPeriodic=0
    g293: BSplineCurve PolesCount=3 KnotsCount=2 Degree=2 IsPeriodic=0
    g294: BSplineCurve PolesCount=3 KnotsCount=2 Degree=2 IsPeriodic=0
    g295: BSplineCurve PolesCount=3 KnotsCount=2 Degree=2 IsPeriodic=0
    g296: BSplineCurve PolesCount=3 KnotsCount=2 Degree=2 IsPeriodic=0
    g297: BSplineCurve PolesCount=3 KnotsCount=2 Degree=2 IsPeriodic=0
    g298: BSplineCurve PolesCount=3 KnotsCount=2 Degree=2 IsPeriodic=0
    g299: BSplineCurve PolesCount=3 KnotsCount=2 Degree=2 IsPeriodic=0
    g300: BSplineCurve PolesCount=3 KnotsCount=2 Degree=2 IsPeriodic=0
    g301: BSplineCurve PolesCount=3 KnotsCount=2 Degree=2 IsPeriodic=0
    g302: BSplineCurve PolesCount=3 KnotsCount=2 Degree=2 IsPeriodic=0
    g303: BSplineCurve PolesCount=3 KnotsCount=2 Degree=2 IsPeriodic=0
    g304: BSplineCurve PolesCount=3 KnotsCount=2 Degree=2 IsPeriodic=0
    g305: BSplineCurve PolesCount=3 KnotsCount=2 Degree=2 IsPeriodic=0
    g306: BSplineCurve PolesCount=3 KnotsCount=2 Degree=2 IsPeriodic=0
    g307: BSplineCurve PolesCount=3 KnotsCount=2 Degree=2 IsPeriodic=0
    g308: BSplineCurve PolesCount=3 KnotsCount=2 Degree=2 IsPeriodic=0
    g309: BSplineCurve PolesCount=3 KnotsCount=2 Degree=2 IsPeriodic=0
    g310: BSplineCurve PolesCount=3 KnotsCount=2 Degree=2 IsPeriodic=0
    g311: BSplineCurve PolesCount=3 KnotsCount=2 Degree=2 IsPeriodic=0
    g312: BSplineCurve PolesCount=3 KnotsCount=2 Degree=2 IsPeriodic=0
    g313: BSplineCurve PolesCount=3 KnotsCount=2 Degree=2 IsPeriodic=0
    g314: BSplineCurve PolesCount=3 KnotsCount=2 Degree=2 IsPeriodic=0
    g315: BSplineCurve PolesCount=3 KnotsCount=2 Degree=2 IsPeriodic=0
    g316: BSplineCurve PolesCount=3 KnotsCount=2 Degree=2 IsPeriodic=0
    g317: BSplineCurve PolesCount=3 KnotsCount=2 Degree=2 IsPeriodic=0
    g318: BSplineCurve PolesCount=3 KnotsCount=2 Degree=2 IsPeriodic=0
    g319: BSplineCurve PolesCount=3 KnotsCount=2 Degree=2 IsPeriodic=0
    g320: BSplineCurve PolesCount=2 KnotsCount=2 Degree=1 IsPeriodic=0
    g321: BSplineCurve PolesCount=3 KnotsCount=2 Degree=2 IsPeriodic=0
    g322: BSplineCurve PolesCount=3 KnotsCount=2 Degree=2 IsPeriodic=0
    g323: BSplineCurve PolesCount=3 KnotsCount=2 Degree=2 IsPeriodic=0
    g324: BSplineCurve PolesCount=3 KnotsCount=2 Degree=2 IsPeriodic=0
    g325: BSplineCurve PolesCount=3 KnotsCount=2 Degree=2 IsPeriodic=0
    g326: BSplineCurve PolesCount=3 KnotsCount=2 Degree=2 IsPeriodic=0
    g327: BSplineCurve PolesCount=3 KnotsCount=2 Degree=2 IsPeriodic=0
    g328: BSplineCurve PolesCount=3 KnotsCount=2 Degree=2 IsPeriodic=0
    g329: BSplineCurve PolesCount=3 KnotsCount=2 Degree=2 IsPeriodic=0
    g330: BSplineCurve PolesCount=3 KnotsCount=2 Degree=2 IsPeriodic=0
    g331: BSplineCurve PolesCount=3 KnotsCount=2 Degree=2 IsPeriodic=0
    g332: BSplineCurve PolesCount=3 KnotsCount=2 Degree=2 IsPeriodic=0
    g333: BSplineCurve PolesCount=3 KnotsCount=2 Degree=2 IsPeriodic=0
    g334: BSplineCurve PolesCount=3 KnotsCount=2 Degree=2 IsPeriodic=0
    g335: BSplineCurve PolesCount=3 KnotsCount=2 Degree=2 IsPeriodic=0
    g336: BSplineCurve PolesCount=3 KnotsCount=2 Degree=2 IsPeriodic=0
    g337: BSplineCurve PolesCount=2 KnotsCount=2 Degree=1 IsPeriodic=0
    g338: BSplineCurve PolesCount=2 KnotsCount=2 Degree=1 IsPeriodic=0
    g339: BSplineCurve PolesCount=2 KnotsCount=2 Degree=1 IsPeriodic=0
    g340: BSplineCurve PolesCount=2 KnotsCount=2 Degree=1 IsPeriodic=0
    g341: BSplineCurve PolesCount=2 KnotsCount=2 Degree=1 IsPeriodic=0
    g342: BSplineCurve PolesCount=2 KnotsCount=2 Degree=1 IsPeriodic=0
    g343: BSplineCurve PolesCount=2 KnotsCount=2 Degree=1 IsPeriodic=0
    g344: BSplineCurve PolesCount=2 KnotsCount=2 Degree=1 IsPeriodic=0
    g345: BSplineCurve PolesCount=2 KnotsCount=2 Degree=1 IsPeriodic=0
    g346: BSplineCurve PolesCount=2 KnotsCount=2 Degree=1 IsPeriodic=0
    g347: BSplineCurve PolesCount=2 KnotsCount=2 Degree=1 IsPeriodic=0
    g348: BSplineCurve PolesCount=3 KnotsCount=2 Degree=2 IsPeriodic=0
    g349: BSplineCurve PolesCount=3 KnotsCount=2 Degree=2 IsPeriodic=0
    g350: BSplineCurve PolesCount=3 KnotsCount=2 Degree=2 IsPeriodic=0
    g351: BSplineCurve PolesCount=3 KnotsCount=2 Degree=2 IsPeriodic=0
    g352: BSplineCurve PolesCount=3 KnotsCount=2 Degree=2 IsPeriodic=0
    g353: BSplineCurve PolesCount=3 KnotsCount=2 Degree=2 IsPeriodic=0
    g354: BSplineCurve PolesCount=3 KnotsCount=2 Degree=2 IsPeriodic=0
    g355: BSplineCurve PolesCount=3 KnotsCount=2 Degree=2 IsPeriodic=0
    g356: BSplineCurve PolesCount=3 KnotsCount=2 Degree=2 IsPeriodic=0
    g357: BSplineCurve PolesCount=3 KnotsCount=2 Degree=2 IsPeriodic=0
    g358: BSplineCurve PolesCount=3 KnotsCount=2 Degree=2 IsPeriodic=0
    g359: BSplineCurve PolesCount=3 KnotsCount=2 Degree=2 IsPeriodic=0
    g360: BSplineCurve PolesCount=3 KnotsCount=2 Degree=2 IsPeriodic=0
    g361: BSplineCurve PolesCount=3 KnotsCount=2 Degree=2 IsPeriodic=0
    g362: BSplineCurve PolesCount=3 KnotsCount=2 Degree=2 IsPeriodic=0
    g363: BSplineCurve PolesCount=3 KnotsCount=2 Degree=2 IsPeriodic=0
    g364: BSplineCurve PolesCount=2 KnotsCount=2 Degree=1 IsPeriodic=0
    g365: BSplineCurve PolesCount=2 KnotsCount=2 Degree=1 IsPeriodic=0
    g366: BSplineCurve PolesCount=2 KnotsCount=2 Degree=1 IsPeriodic=0
    g367: BSplineCurve PolesCount=2 KnotsCount=2 Degree=1 IsPeriodic=0
    g368: BSplineCurve PolesCount=2 KnotsCount=2 Degree=1 IsPeriodic=0
    g369: BSplineCurve PolesCount=2 KnotsCount=2 Degree=1 IsPeriodic=0
    g370: BSplineCurve PolesCount=2 KnotsCount=2 Degree=1 IsPeriodic=0
    g371: BSplineCurve PolesCount=2 KnotsCount=2 Degree=1 IsPeriodic=0
    g372: BSplineCurve PolesCount=2 KnotsCount=2 Degree=1 IsPeriodic=0
    g373: BSplineCurve PolesCount=2 KnotsCount=2 Degree=1 IsPeriodic=0
    g374: BSplineCurve PolesCount=2 KnotsCount=2 Degree=1 IsPeriodic=0
    g375: BSplineCurve PolesCount=2 KnotsCount=2 Degree=1 IsPeriodic=0
    g376: BSplineCurve PolesCount=2 KnotsCount=2 Degree=1 IsPeriodic=0
    g377: BSplineCurve PolesCount=2 KnotsCount=2 Degree=1 IsPeriodic=0
    g378: BSplineCurve PolesCount=2 KnotsCount=2 Degree=1 IsPeriodic=0
    g379: BSplineCurve PolesCount=2 KnotsCount=2 Degree=1 IsPeriodic=0
    g380: BSplineCurve PolesCount=2 KnotsCount=2 Degree=1 IsPeriodic=0
    g381: BSplineCurve PolesCount=2 KnotsCount=2 Degree=1 IsPeriodic=0
    g382: BSplineCurve PolesCount=2 KnotsCount=2 Degree=1 IsPeriodic=0
    g383: BSplineCurve PolesCount=2 KnotsCount=2 Degree=1 IsPeriodic=0
    g384: BSplineCurve PolesCount=2 KnotsCount=2 Degree=1 IsPeriodic=0
    g385: BSplineCurve PolesCount=2 KnotsCount=2 Degree=1 IsPeriodic=0
    g386: BSplineCurve PolesCount=2 KnotsCount=2 Degree=1 IsPeriodic=0
    g387: BSplineCurve PolesCount=2 KnotsCount=2 Degree=1 IsPeriodic=0
    g388: BSplineCurve PolesCount=2 KnotsCount=2 Degree=1 IsPeriodic=0
    g389: BSplineCurve PolesCount=2 KnotsCount=2 Degree=1 IsPeriodic=0
    g390: BSplineCurve PolesCount=2 KnotsCount=2 Degree=1 IsPeriodic=0
    g391: BSplineCurve PolesCount=2 KnotsCount=2 Degree=1 IsPeriodic=0
    g392: BSplineCurve PolesCount=2 KnotsCount=2 Degree=1 IsPeriodic=0
    g393: BSplineCurve PolesCount=2 KnotsCount=2 Degree=1 IsPeriodic=0
    g394: BSplineCurve PolesCount=2 KnotsCount=2 Degree=1 IsPeriodic=0
    g395: BSplineCurve PolesCount=2 KnotsCount=2 Degree=1 IsPeriodic=0
    g396: BSplineCurve PolesCount=2 KnotsCount=2 Degree=1 IsPeriodic=0
    g397: BSplineCurve PolesCount=2 KnotsCount=2 Degree=1 IsPeriodic=0
    g398: BSplineCurve PolesCount=3 KnotsCount=2 Degree=2 IsPeriodic=0
    g399: BSplineCurve PolesCount=3 KnotsCount=2 Degree=2 IsPeriodic=0
    ... +790 more geometry lines
  constraints (1190):
    c: Coincident(g93,g94)
    c: Coincident(g92,g93)
    c: Coincident(g282,g284)
    c: Coincident(g273,g274)
    c: Coincident(g272,g273)
    c: Coincident(g280,g282)
    c: Coincident(g88,g89)
    c: Coincident(g96,g97)
    c: Coincident(g299,g300)
    c: Coincident(g284,g286)
    c: Coincident(g298,g299)
    c: Coincident(g96,g99)
    c: Coincident(g89,g90)
    c: Coincident(g280,g281)
    c: Coincident(g271,g272)
    c: Coincident(g298,g304)
    c: Coincident(g300,g301)
    c: Coincident(g286,g288)
    c: Coincident(g274,g275)
    c: Coincident(g281,g283)
    c: Coincident(g303,g304)
    c: Coincident(g301,g302)
    c: Coincident(g288,g290)
    c: Coincident(g302,g303)
    c: Coincident(g283,g285)
    c: Coincident(g285,g287)
    c: Coincident(g290,g292)
    c: Coincident(g292,g294)
    c: Coincident(g270,g271)
    c: Coincident(g306,g308)
    c: Coincident(g287,g289)
    c: Coincident(g249,g251)
    c: Coincident(g314,g316)
    c: Coincident(g305,g306)
    c: Coincident(g308,g310)
    c: Coincident(g294,g296)
    c: Coincident(g251,g253)
    c: Coincident(g312,g314)
    c: Coincident(g263,g264)
    c: Coincident(g322,g324)
    c: Coincident(g316,g318)
    c: Coincident(g264,g265)
    c: Coincident(g289,g291)
    c: Coincident(g305,g307)
    c: Coincident(g324,g326)
    c: Coincident(g247,g249)
    c: Coincident(g310,g311)
    c: Coincident(g296,g297)
    c: Coincident(g262,g263)
    c: Coincident(g276,g277)
    c: Coincident(g320,g322)
    c: Coincident(g318,g320)
    c: Coincident(g265,g266)
    c: Coincident(g309,g311)
    c: Coincident(g275,g276)
    c: Coincident(g307,g309)
    c: Coincident(g291,g293)
    c: Coincident(g270,g279)
    c: Coincident(g325,g327)
    c: Coincident(g323,g325)
    c: Coincident(g100,g101)
    c: Coincident(g84,g85)
    c: Coincident(g253,g255)
    c: Coincident(g295,g297)
    c: Coincident(g277,g278)
    c: Coincident(g262,g269)
    c: Coincident(g312,g313)
    c: Coincident(g326,g327)
    c: Coincident(g247,g248)
    c: Coincident(g293,g295)
    c: Coincident(g329,g330)
    c: Coincident(g330,g331)
    c: Coincident(g278,g279)
    c: Coincident(g254,g256)
    c: Coincident(g266,g267)
    c: Coincident(g85,g86)
    c: Coincident(g100,g103)
    c: Coincident(g328,g329)
    c: Coincident(g321,g323)
    c: Coincident(g268,g269)
    c: Coincident(g267,g268)
    c: Coincident(g331,g332)
    c: Coincident(g94,g95)
    c: Coincident(g92,g95)
    c: Coincident(g252,g254)
    c: Coincident(g328,g336)
    c: Coincident(g248,g250)
    c: Coincident(g250,g252)
    c: Coincident(g332,g333)
    c: Coincident(g256,g258)
    c: Coincident(g319,g321)
    c: Coincident(g335,g336)
    c: Coincident(g255,g257)
    c: Coincident(g313,g315)
    c: Coincident(g88,g91)
    c: Coincident(g97,g98)
    c: Coincident(g260,g261)
    c: Coincident(g98,g99)
    c: Coincident(g90,g91)
    c: Coincident(g333,g334)
    c: Coincident(g259,g261)
    c: Coincident(g334,g335)
    c: Coincident(g258,g260)
    c: Coincident(g317,g319)
    c: Coincident(g348,g350)
    c: Coincident(g350,g352)
    c: Coincident(g315,g317)
    c: Coincident(g257,g259)
    c: Coincident(g357,g358)
    c: Coincident(g356,g357)
    c: Coincident(g228,g229)
    c: Coincident(g227,g228)
    c: Coincident(g346,g347)
    c: Coincident(g229,g230)
    c: Coincident(g352,g354)
    c: Coincident(g358,g359)
    c: Coincident(g231,g232)
    c: Coincident(g348,g349)
    c: Coincident(g230,g231)
    c: Coincident(g345,g346)
    c: Coincident(g356,g363)
    c: Coincident(g226,g227)
    c: Coincident(g232,g233)
    c: Coincident(g344,g345)
    c: Coincident(g238,g239)
    c: Coincident(g338,g339)
    c: Coincident(g237,g238)
    c: Coincident(g337,g347)
    c: Coincident(g359,g360)
    c: Coincident(g233,g234)
    c: Coincident(g236,g237)
    c: Coincident(g101,g102)
    c: Coincident(g84,g87)
    c: Coincident(g354,g355)
    c: Coincident(g243,g244)
    c: Coincident(g337,g338)
    c: Coincident(g362,g363)
    c: Coincident(g226,g246)
    c: Coincident(g349,g351)
    c: Coincident(g235,g236)
    c: Coincident(g234,g235)
    c: Coincident(g102,g103)
    c: Coincident(g86,g87)
    c: Coincident(g244,g245)
    c: Coincident(g80,g81)
    c: Coincident(g104,g105)
    c: Coincident(g245,g246)
    c: Coincident(g360,g361)
    c: Coincident(g361,g362)
    c: Coincident(g351,g353)
    c: Coincident(g242,g243)
    c: Coincident(g353,g355)
    c: Coincident(g239,g240)
    c: Coincident(g81,g82)
    c: Coincident(g104,g107)
    c: Coincident(g241,g242)
    c: Coincident(g340,g341)
    c: Coincident(g339,g340)
    c: Coincident(g240,g241)
    c: Coincident(g343,g344)
    c: Coincident(g341,g342)
    c: Coincident(g342,g343)
    c: Coincident(g384,g385)
    c: Coincident(g383,g384)
    c: Coincident(g382,g383)
    c: Coincident(g376,g377)
    c: Coincident(g214,g216)
    c: Coincident(g375,g385)
    c: Coincident(g373,g374)
    c: Coincident(g216,g218)
    c: Coincident(g80,g83)
    c: Coincident(g105,g106)
    c: Coincident(g375,g376)
    c: Coincident(g210,g212)
    c: Coincident(g220,g221)
    c: Coincident(g372,g373)
    c: Coincident(g221,g222)
    c: Coincident(g208,g210)
    c: Coincident(g222,g223)
    c: Coincident(g106,g107)
    c: Coincident(g82,g83)
    c: Coincident(g212,g214)
    c: Coincident(g371,g372)
    c: Coincident(g208,g209)
    c: Coincident(g219,g220)
    c: Coincident(g365,g366)
    c: Coincident(g213,g215)
    c: Coincident(g209,g211)
    c: Coincident(g364,g374)
    c: Coincident(g377,g378)
    c: Coincident(g211,g213)
    c: Coincident(g364,g365)
    c: Coincident(g381,g382)
    c: Coincident(g378,g379)
    c: Coincident(g380,g381)
    c: Coincident(g379,g380)
    c: Coincident(g223,g224)
    c: Coincident(g224,g225)
    c: Coincident(g219,g225)
    c: Coincident(g217,g218)
    c: Coincident(g108,g109)
    c: Coincident(g76,g77)
    c: Coincident(g215,g217)
    c: Coincident(g366,g367)
    c: Coincident(g370,g371)
    c: Coincident(g367,g368)
    c: Coincident(g369,g370)
    c: Coincident(g368,g369)
    c: Coincident(g108,g111)
    c: Coincident(g77,g78)
    c: Coincident(g419,g420)
    c: Coincident(g418,g419)
    c: Coincident(g109,g110)
    c: Coincident(g76,g79)
    c: Coincident(g78,g79)
    c: Coincident(g110,g111)
    c: Coincident(g181,g182)
    c: Coincident(g414,g415)
    c: Coincident(g413,g414)
    c: Coincident(g415,g416)
    c: Coincident(g182,g183)
    c: Coincident(g417,g418)
    c: Coincident(g412,g413)
    c: Coincident(g416,g417)
    c: Coincident(g397,g420)
    c: Coincident(g401,g402)
    c: Coincident(g402,g403)
    c: Coincident(g400,g401)
    c: Coincident(g180,g181)
    c: Coincident(g397,g398)
    c: Coincident(g183,g184)
    c: Coincident(g403,g404)
    c: Coincident(g399,g400)
    c: Coincident(g398,g399)
    c: Coincident(g395,g396)
    c: Coincident(g184,g185)
    c: Coincident(g411,g412)
    c: Coincident(g394,g395)
    c: Coincident(g404,g405)
    c: Coincident(g189,g190)
    c: Coincident(g185,g186)
    c: Coincident(g198,g199)
    c: Coincident(g179,g180)
    c: Coincident(g188,g189)
    c: Coincident(g405,g406)
    c: Coincident(g190,g191)
    c: Coincident(g407,g408)
    c: Coincident(g393,g394)
    c: Coincident(g197,g198)
    c: Coincident(g191,g192)
    c: Coincident(g410,g411)
    c: Coincident(g406,g407)
    c: Coincident(g186,g187)
    c: Coincident(g187,g188)
    c: Coincident(g205,g206)
    c: Coincident(g204,g205)
    c: Coincident(g387,g388)
    c: Coincident(g408,g409)
    c: Coincident(g199,g200)
    c: Coincident(g179,g207)
    c: Coincident(g196,g197)
    c: Coincident(g409,g410)
    c: Coincident(g192,g193)
    c: Coincident(g206,g207)
    c: Coincident(g386,g396)
    c: Coincident(g195,g196)
    c: Coincident(g203,g204)
    c: Coincident(g386,g387)
    c: Coincident(g193,g194)
    c: Coincident(g200,g201)
    c: Coincident(g194,g195)
    c: Coincident(g202,g203)
    c: Coincident(g201,g202)
    c: Coincident(g392,g393)
    c: Coincident(g388,g389)
    c: Coincident(g391,g392)
    c: Coincident(g389,g390)
    c: Coincident(g112,g113)
    c: Coincident(g72,g73)
    c: Coincident(g390,g391)
    c: Coincident(g73,g74)
    c: Coincident(g112,g115)
    c: Coincident(g72,g75)
    c: Coincident(g113,g114)
    c: Coincident(g432,g433)
    c: Coincident(g432,g460)
    c: Coincident(g74,g75)
    c: Coincident(g114,g115)
    c: Coincident(g438,g439)
    c: Coincident(g439,g440)
    c: Coincident(g459,g460)
    c: Coincident(g433,g434)
    c: Coincident(g437,g438)
    c: Coincident(g456,g457)
    c: Coincident(g440,g441)
    c: Coincident(g155,g178)
    c: Coincident(g455,g456)
    c: Coincident(g155,g156)
    c: Coincident(g458,g459)
    c: Coincident(g457,g458)
    c: Coincident(g445,g446)
    c: Coincident(g446,g447)
    c: Coincident(g434,g435)
    c: Coincident(g175,g176)
    c: Coincident(g454,g455)
    c: Coincident(g441,g442)
    c: Coincident(g156,g157)
    c: Coincident(g447,g448)
    c: Coincident(g444,g445)
    c: Coincident(g442,g443)
    c: Coincident(g436,g437)
    c: Coincident(g174,g175)
    c: Coincident(g443,g444)
    c: Coincident(g157,g158)
    c: Coincident(g430,g431)
    c: Coincident(g166,g167)
    c: Coincident(g435,g436)
    c: Coincident(g448,g449)
    c: Coincident(g429,g430)
    c: Coincident(g453,g454)
    c: Coincident(g173,g174)
    c: Coincident(g450,g451)
    c: Coincident(g449,g450)
    c: Coincident(g165,g166)
    c: Coincident(g158,g159)
    c: Coincident(g167,g168)
    c: Coincident(g164,g165)
    c: Coincident(g451,g452)
    c: Coincident(g452,g453)
    c: Coincident(g177,g178)
    c: Coincident(g159,g160)
    c: Coincident(g428,g429)
    c: Coincident(g176,g177)
    c: Coincident(g172,g173)
    c: Coincident(g163,g164)
    c: Coincident(g160,g161)
    c: Coincident(g422,g423)
    c: Coincident(g168,g169)
    c: Coincident(g161,g162)
    c: Coincident(g162,g163)
    c: Coincident(g171,g172)
    c: Coincident(g421,g431)
    c: Coincident(g170,g171)
    c: Coincident(g169,g170)
    c: Coincident(g421,g422)
    c: Coincident(g427,g428)
    c: Coincident(g423,g424)
    c: Coincident(g426,g427)
    c: Coincident(g424,g425)
    c: Coincident(g425,g426)
    c: Coincident(g68,g69)
    c: Coincident(g116,g117)
    c: Coincident(g116,g119)
    c: Coincident(g69,g70)
    c: Coincident(g68,g71)
    c: Coincident(g117,g118)
    c: Coincident(g118,g119)
    c: Coincident(g70,g71)
    c: Coincident(g473,g475)
    c: Coincident(g475,g477)
    c: Coincident(g472,g474)
    c: Coincident(g472,g473)
    c: Coincident(g477,g479)
    c: Coincident(g474,g476)
    c: Coincident(g476,g478)
    c: Coincident(g483,g484)
    c: Coincident(g479,g481)
    c: Coincident(g144,g154)
    c: Coincident(g144,g145)
    c: Coincident(g483,g489)
    c: Coincident(g488,g489)
    c: Coincident(g487,g488)
    c: Coincident(g481,g482)
    c: Coincident(g486,g487)
    c: Coincident(g485,g486)
    c: Coincident(g484,g485)
    c: Coincident(g147,g148)
    c: Coincident(g148,g149)
    c: Coincident(g145,g146)
    c: Coincident(g478,g480)
    c: Coincident(g480,g482)
    c: Coincident(g470,g471)
    c: Coincident(g469,g470)
    c: Coincident(g151,g152)
    c: Coincident(g146,g147)
    c: Coincident(g149,g150)
    c: Coincident(g153,g154)
    c: Coincident(g468,g469)
    c: Coincident(g152,g153)
    c: Coincident(g150,g151)
    c: Coincident(g462,g463)
    c: Coincident(g467,g468)
    c: Coincident(g461,g471)
    c: Coincident(g463,g464)
    c: Coincident(g461,g462)
    c: Coincident(g466,g467)
    c: Coincident(g464,g465)
    c: Coincident(g465,g466)
    c: Coincident(g64,g65)
    c: Coincident(g120,g121)
    c: Coincident(g121,g122)
    c: Coincident(g64,g67)
    c: Coincident(g120,g123)
    c: Coincident(g65,g66)
    c: Coincident(g122,g123)
    c: Coincident(g66,g67)
    c: Coincident(g501,g521)
    c: Coincident(g501,g502)
    c: Coincident(g520,g521)
    c: Coincident(g516,g517)
    c: Coincident(g515,g516)
    c: Coincident(g508,g509)
    c: Coincident(g507,g508)
    c: Coincident(g509,g510)
    c: Coincident(g502,g503)
    c: Coincident(g506,g507)
    c: Coincident(g519,g520)
    c: Coincident(g510,g511)
    c: Coincident(g134,g135)
    c: Coincident(g511,g512)
    c: Coincident(g132,g134)
    c: Coincident(g133,g135)
    c: Coincident(g139,g140)
    c: Coincident(g512,g513)
    c: Coincident(g505,g506)
    c: Coincident(g503,g504)
    c: Coincident(g518,g519)
    c: Coincident(g517,g518)
    c: Coincident(g138,g139)
    c: Coincident(g140,g141)
    c: Coincident(g513,g514)
    c: Coincident(g504,g505)
    c: Coincident(g514,g515)
    c: Coincident(g130,g132)
    c: Coincident(g137,g138)
    c: Coincident(g499,g500)
    c: Coincident(g498,g499)
    c: Coincident(g141,g142)
    c: Coincident(g131,g133)
    c: Coincident(g136,g137)
    c: Coincident(g142,g143)
    c: Coincident(g136,g143)
    c: Coincident(g128,g130)
    c: Coincident(g497,g498)
    c: Coincident(g129,g131)
    c: Coincident(g128,g129)
    c: Coincident(g496,g497)
    c: Coincident(g491,g492)
    c: Coincident(g492,g493)
    c: Coincident(g495,g496)
    c: Coincident(g490,g500)
    c: Coincident(g490,g491)
    c: Coincident(g493,g494)
    c: Coincident(g494,g495)
    c: Coincident(g124,g125)
    c: Coincident(g125,g126)
    c: Coincident(g60,g61)
    c: Coincident(g61,g62)
    c: Coincident(g60,g63)
    c: Coincident(g62,g63)
    c: Coincident(g124,g127)
    c: Coincident(g126,g127)
    c: Coincident(g1169,g1170)
    c: Coincident(g545,g547)
    c: Coincident(g1153,g1154)
    c: Coincident(g533,g534)
    c: Coincident(g1170,g1171)
    c: Coincident(g534,g536)
    c: Coincident(g1168,g1169)
    c: Coincident(g546,g547)
    c: Coincident(g533,g535)
    c: Coincident(g1152,g1153)
    c: Coincident(g548,g555)
    c: Coincident(g1154,g1155)
    c: Coincident(g1167,g1168)
    c: Coincident(g554,g555)
    c: Coincident(g548,g549)
    c: Coincident(g1161,g1162)
    c: Coincident(g1160,g1161)
    c: Coincident(g543,g545)
    c: Coincident(g544,g546)
    c: Coincident(g1171,g1172)
    c: Coincident(g536,g538)
    c: Coincident(g1166,g1167)
    c: Coincident(g1162,g1163)
    c: Coincident(g1159,g1160)
    c: Coincident(g553,g554)
    c: Coincident(g549,g550)
    c: Coincident(g535,g537)
    c: Coincident(g1155,g1156)
    c: Coincident(g1151,g1152)
    c: Coincident(g538,g540)
    c: Coincident(g1165,g1166)
    c: Coincident(g1175,g1176)
    c: Coincident(g1176,g1177)
    c: Coincident(g542,g544)
    c: Coincident(g1163,g1164)
    c: Coincident(g552,g553)
    c: Coincident(g1158,g1159)
    c: Coincident(g1164,g1165)
    c: Coincident(g550,g551)
    c: Coincident(g1172,g1173)
    c: Coincident(g1156,g1157)
    c: Coincident(g541,g543)
    c: Coincident(g540,g542)
    c: Coincident(g551,g552)
    c: Coincident(g1157,g1158)
    c: Coincident(g1174,g1175)
    c: Coincident(g537,g539)
    c: Coincident(g1177,g1178)
    c: Coincident(g1173,g1174)
    c: Coincident(g1150,g1151)
    c: Coincident(g539,g541)
    c: Coincident(g1150,g1178)
    c: Coincident(g1183,g1184)
    c: Coincident(g530,g531)
    c: Coincident(g1182,g1183)
    c: Coincident(g531,g532)
    c: Coincident(g1179,g1180)
    c: Coincident(g1179,g1189)
    c: Coincident(g528,g529)
    c: Coincident(g1184,g1185)
    c: Coincident(g1181,g1182)
    c: Coincident(g529,g530)
    c: Coincident(g527,g528)
    c: Coincident(g1180,g1181)
    c: Coincident(g524,g525)
    c: Coincident(g1185,g1186)
    c: Coincident(g523,g524)
    c: Coincident(g1186,g1187)
    c: Coincident(g526,g527)
    c: Coincident(g525,g526)
    c: Coincident(g522,g523)
    c: Coincident(g522,g532)
    c: Coincident(g1187,g1188)
    c: Coincident(g1188,g1189)
    c: Coincident(g56,g57)
    c: Coincident(g0,g1)
    c: Coincident(g0,g3)
    c: Coincident(g57,g58)
    c: Coincident(g1,g2)
    c: Coincident(g56,g59)
    c: Coincident(g2,g3)
    c: Coincident(g58,g59)
    c: Coincident(g575,g576)
    c: Coincident(g567,g576)
    c: Coincident(g1124,g1125)
    c: Coincident(g1125,g1126)
    c: Coincident(g572,g573)
    c: Coincident(g1123,g1124)
    c: Coincident(g1108,g1109)
    c: Coincident(g1122,g1123)
    c: Coincident(g1126,g1127)
    c: Coincident(g1109,g1110)
    c: Coincident(g1121,g1122)
    c: Coincident(g1116,g1117)
    c: Coincident(g567,g568)
    c: Coincident(g1107,g1108)
    c: Coincident(g1115,g1116)
    c: Coincident(g1117,g1118)
    c: Coincident(g1114,g1115)
    c: Coincident(g1120,g1121)
    c: Coincident(g568,g569)
    c: Coincident(g1118,g1119)
    c: Coincident(g571,g572)
    c: Coincident(g1127,g1128)
    c: Coincident(g1130,g1131)
    c: Coincident(g1131,g1132)
    c: Coincident(g1119,g1120)
    c: Coincident(g1110,g1111)
    c: Coincident(g1106,g1107)
    c: Coincident(g569,g570)
    c: Coincident(g1113,g1114)
    c: Coincident(g574,g575)
    c: Coincident(g573,g574)
    c: Coincident(g1129,g1130)
    c: Coincident(g1128,g1129)
    c: Coincident(g1111,g1112)
    c: Coincident(g1112,g1113)
    c: Coincident(g570,g571)
    c: Coincident(g1132,g1133)
    c: Coincident(g1105,g1106)
    c: Coincident(g1105,g1133)
    c: Coincident(g1139,g1141)
    c: Coincident(g1140,g1141)
    c: Coincident(g1146,g1147)
    c: Coincident(g562,g563)
    c: Coincident(g1145,g1146)
    c: Coincident(g564,g565)
    c: Coincident(g565,g566)
    c: Coincident(g1137,g1139)
    c: Coincident(g1138,g1140)
    c: Coincident(g561,g562)
    c: Coincident(g1147,g1148)
    c: Coincident(g558,g559)
    c: Coincident(g1144,g1145)
    c: Coincident(g563,g564)
    c: Coincident(g1148,g1149)
    c: Coincident(g1143,g1144)
    c: Coincident(g1135,g1137)
    c: Coincident(g1136,g1138)
    c: Coincident(g557,g558)
    c: Coincident(g560,g561)
    c: Coincident(g559,g560)
    c: Coincident(g1142,g1149)
    c: Coincident(g1142,g1143)
    c: Coincident(g1134,g1135)
    c: Coincident(g1134,g1136)
    c: Coincident(g556,g557)
    c: Coincident(g556,g566)
    c: Coincident(g4,g5)
    c: Coincident(g52,g53)
    c: Coincident(g5,g6)
    c: Coincident(g52,g55)
    c: Coincident(g53,g54)
    c: Coincident(g4,g7)
    c: Coincident(g54,g55)
    c: Coincident(g6,g7)
    c: Coincident(g599,g601)
    c: Coincident(g1068,g1069)
    c: Coincident(g1067,g1068)
    c: Coincident(g597,g599)
    c: Coincident(g1065,g1066)
    c: Coincident(g595,g597)
    c: Coincident(g1066,g1067)
    c: Coincident(g613,g615)
    c: Coincident(g601,g603)
    c: Coincident(g1069,g1070)
    c: Coincident(g589,g591)
    c: Coincident(g588,g589)
    c: Coincident(g615,g617)
    c: Coincident(g1064,g1065)
    c: Coincident(g613,g614)
    c: Coincident(g593,g595)
    c: Coincident(g591,g593)
    c: Coincident(g611,g612)
    c: Coincident(g1056,g1057)
    c: Coincident(g1057,g1058)
    c: Coincident(g606,g612)
    c: Coincident(g1056,g1079)
    c: Coincident(g617,g619)
    c: Coincident(g1063,g1064)
    c: Coincident(g1058,g1059)
    c: Coincident(g614,g616)
    c: Coincident(g588,g590)
    c: Coincident(g603,g605)
    c: Coincident(g1070,g1071)
    c: Coincident(g1059,g1060)
    c: Coincident(g610,g611)
    c: Coincident(g1076,g1077)
    c: Coincident(g1075,g1076)
    c: Coincident(g606,g607)
    c: Coincident(g618,g619)
    c: Coincident(g1062,g1063)
    c: Coincident(g1060,g1061)
    c: Coincident(g616,g618)
    c: Coincident(g1061,g1062)
    c: Coincident(g1074,g1075)
    c: Coincident(g600,g602)
    c: Coincident(g598,g600)
    c: Coincident(g604,g605)
    c: Coincident(g1071,g1072)
    c: Coincident(g609,g610)
    c: Coincident(g1073,g1074)
    c: Coincident(g602,g604)
    c: Coincident(g607,g608)
    c: Coincident(g1072,g1073)
    c: Coincident(g590,g592)
    c: Coincident(g596,g598)
    c: Coincident(g608,g609)
    c: Coincident(g1085,g1087)
    c: Coincident(g1087,g1089)
    c: Coincident(g583,g584)
    c: Coincident(g594,g596)
    c: Coincident(g1101,g1102)
    c: Coincident(g592,g594)
    c: Coincident(g1100,g1101)
    c: Coincident(g1083,g1085)
    c: Coincident(g1077,g1078)
    c: Coincident(g582,g583)
    c: Coincident(g1102,g1103)
    c: Coincident(g1089,g1091)
    c: Coincident(g1078,g1079)
    c: Coincident(g579,g580)
    c: Coincident(g1099,g1100)
    c: Coincident(g1086,g1088)
    c: Coincident(g585,g586)
    c: Coincident(g586,g587)
    c: Coincident(g1088,g1090)
    c: Coincident(g1103,g1104)
    c: Coincident(g1098,g1099)
    c: Coincident(g1084,g1086)
    c: Coincident(g1081,g1083)
    c: Coincident(g1091,g1093)
    c: Coincident(g581,g582)
    c: Coincident(g1097,g1098)
    c: Coincident(g584,g585)
    c: Coincident(g1096,g1104)
    c: Coincident(g580,g581)
    c: Coincident(g1096,g1097)
    c: Coincident(g1093,g1095)
    c: Coincident(g1090,g1092)
    c: Coincident(g1094,g1095)
    c: Coincident(g578,g579)
    c: Coincident(g1082,g1084)
    c: Coincident(g1092,g1094)
    c: Coincident(g1080,g1081)
    c: Coincident(g48,g49)
    c: Coincident(g8,g9)
    c: Coincident(g1080,g1082)
    c: Coincident(g577,g578)
    c: Coincident(g577,g587)
    c: Coincident(g9,g10)
    c: Coincident(g48,g51)
    c: Coincident(g8,g11)
    c: Coincident(g49,g50)
    c: Coincident(g1012,g1013)
    c: Coincident(g632,g634)
    c: Coincident(g50,g51)
    c: Coincident(g10,g11)
    c: Coincident(g1011,g1012)
    c: Coincident(g1009,g1010)
    c: Coincident(g1013,g1014)
    c: Coincident(g634,g636)
    c: Coincident(g654,g655)
    c: Coincident(g1010,g1011)
    c: Coincident(g631,g632)
    c: Coincident(g1008,g1009)
    c: Coincident(g653,g654)
    c: Coincident(g647,g655)
    c: Coincident(g647,g648)
    c: Coincident(g645,g646)
    c: Coincident(g1007,g1008)
    c: Coincident(g652,g653)
    c: Coincident(g1014,g1015)
    c: Coincident(g636,g638)
    c: Coincident(g648,g649)
    c: Coincident(g1001,g1002)
    c: Coincident(g644,g646)
    c: Coincident(g1002,g1003)
    c: Coincident(g1006,g1007)
    c: Coincident(g1000,g1001)
    c: Coincident(g1003,g1004)
    c: Coincident(g1005,g1006)
    c: Coincident(g1004,g1005)
    c: Coincident(g649,g650)
    c: Coincident(g651,g652)
    c: Coincident(g631,g633)
    c: Coincident(g1000,g1023)
    c: Coincident(g643,g645)
    c: Coincident(g1019,g1020)
    c: Coincident(g1015,g1016)
    c: Coincident(g1020,g1021)
    c: Coincident(g1018,g1019)
    c: Coincident(g650,g651)
    c: Coincident(g642,g644)
    c: Coincident(g1016,g1017)
    c: Coincident(g638,g640)
    c: Coincident(g1017,g1018)
    c: Coincident(g1039,g1041)
    c: Coincident(g1040,g1041)
    c: Coincident(g626,g627)
    c: Coincident(g640,g642)
    c: Coincident(g1053,g1055)
    c: Coincident(g641,g643)
    c: Coincident(g1037,g1039)
    c: Coincident(g1054,g1055)
    c: Coincident(g625,g626)
    c: Coincident(g639,g641)
    c: Coincident(g633,g635)
    c: Coincident(g1038,g1040)
    c: Coincident(g1051,g1053)
    c: Coincident(g622,g623)
    c: Coincident(g637,g639)
    c: Coincident(g1032,g1034)
    c: Coincident(g1052,g1054)
    c: Coincident(g635,g637)
    c: Coincident(g1036,g1038)
    c: Coincident(g1034,g1036)
    c: Coincident(g1030,g1032)
    c: Coincident(g1021,g1022)
    c: Coincident(g1035,g1037)
    c: Coincident(g1045,g1046)
    c: Coincident(g1022,g1023)
    c: Coincident(g1050,g1052)
    c: Coincident(g1044,g1045)
    c: Coincident(g1049,g1051)
    c: Coincident(g624,g625)
    c: Coincident(g628,g629)
    c: Coincident(g1046,g1047)
    c: Coincident(g1049,g1050)
    c: Coincident(g629,g630)
    c: Coincident(g623,g624)
    c: Coincident(g1033,g1035)
    c: Coincident(g1028,g1030)
    c: Coincident(g1029,g1031)
    c: Coincident(g1027,g1029)
    c: Coincident(g1031,g1033)
    c: Coincident(g1047,g1048)
    c: Coincident(g12,g13)
    c: Coincident(g44,g45)
    c: Coincident(g627,g628)
    c: Coincident(g1025,g1027)
    c: Coincident(g1043,g1044)
    c: Coincident(g621,g622)
    c: Coincident(g1042,g1048)
    c: Coincident(g1026,g1028)
    c: Coincident(g1042,g1043)
    c: Coincident(g44,g47)
    c: Coincident(g13,g14)
    c: Coincident(g1024,g1025)
    c: Coincident(g1024,g1026)
    c: Coincident(g620,g621)
    c: Coincident(g620,g630)
    c: Coincident(g978,g979)
    c: Coincident(g681,g683)
    c: Coincident(g45,g46)
    c: Coincident(g12,g15)
    c: Coincident(g977,g978)
    c: Coincident(g683,g685)
    c: Coincident(g979,g980)
    c: Coincident(g975,g976)
    c: Coincident(g694,g695)
    c: Coincident(g693,g694)
    c: Coincident(g974,g975)
    c: Coincident(g976,g977)
    c: Coincident(g680,g681)
    c: Coincident(g14,g15)
    c: Coincident(g46,g47)
    c: Coincident(g973,g974)
    c: Coincident(g980,g981)
    c: Coincident(g688,g695)
    c: Coincident(g692,g693)
    c: Coincident(g685,g687)
    c: Coincident(g997,g998)
    c: Coincident(g972,g973)
    c: Coincident(g971,g972)
    c: Coincident(g996,g997)
    c: Coincident(g981,g982)
    c: Coincident(g670,g671)
    c: Coincident(g970,g971)
    c: Coincident(g969,g970)
    c: Coincident(g968,g969)
    c: Coincident(g967,g968)
    c: Coincident(g982,g983)
    c: Coincident(g966,g967)
    c: Coincident(g669,g670)
    c: Coincident(g983,g984)
    c: Coincident(g671,g672)
    c: Coincident(g680,g682)
    c: Coincident(g688,g689)
    c: Coincident(g984,g985)
    c: Coincident(g691,g692)
    c: Coincident(g663,g664)
    c: Coincident(g985,g986)
    c: Coincident(g966,g989)
    c: Coincident(g986,g987)
    c: Coincident(g664,g665)
    c: Coincident(g662,g663)
    c: Coincident(g686,g687)
    c: Coincident(g672,g673)
    c: Coincident(g668,g669)
    c: Coincident(g665,g666)
    c: Coincident(g661,g662)
    c: Coincident(g689,g690)
    c: Coincident(g998,g999)
    c: Coincident(g995,g996)
    c: Coincident(g690,g691)
    c: Coincident(g673,g674)
    c: Coincident(g682,g684)
    c: Coincident(g990,g999)
    c: Coincident(g660,g661)
    c: Coincident(g40,g41)
    c: Coincident(g16,g17)
    c: Coincident(g666,g667)
    c: Coincident(g684,g686)
    c: Coincident(g987,g988)
    c: Coincident(g667,g668)
    c: Coincident(g994,g995)
    c: Coincident(g990,g991)
    c: Coincident(g659,g660)
    c: Coincident(g988,g989)
    c: Coincident(g677,g678)
    c: Coincident(g17,g18)
    c: Coincident(g40,g43)
    c: Coincident(g674,g675)
    c: Coincident(g678,g679)
    c: Coincident(g991,g992)
    c: Coincident(g658,g659)
    c: Coincident(g993,g994)
    c: Coincident(g675,g676)
    c: Coincident(g657,g658)
    c: Coincident(g992,g993)
    c: Coincident(g676,g677)
    c: Coincident(g656,g657)
    c: Coincident(g656,g679)
    c: Coincident(g931,g932)
    c: Coincident(g726,g727)
    c: Coincident(g932,g933)
    c: Coincident(g725,g726)
    c: Coincident(g928,g929)
    c: Coincident(g930,g931)
    c: Coincident(g927,g928)
    c: Coincident(g722,g723)
    c: Coincident(g929,g930)
    c: Coincident(g933,g934)
    c: Coincident(g926,g927)
    c: Coincident(g724,g725)
    c: Coincident(g41,g42)
    c: Coincident(g16,g19)
    c: Coincident(g925,g926)
    c: Coincident(g710,g711)
    c: Coincident(g709,g710)
    c: Coincident(g723,g724)
    c: Coincident(g934,g935)
    c: Coincident(g951,g953)
    c: Coincident(g953,g955)
    c: Coincident(g924,g925)
    c: Coincident(g703,g704)
    c: Coincident(g923,g924)
    c: Coincident(g42,g43)
    c: Coincident(g18,g19)
    c: Coincident(g704,g705)
    c: Coincident(g711,g712)
    c: Coincident(g935,g936)
    c: Coincident(g954,g956)
    c: Coincident(g922,g923)
    c: Coincident(g952,g954)
    c: Coincident(g921,g922)
    c: Coincident(g702,g703)
    c: Coincident(g936,g937)
    c: Coincident(g36,g37)
    c: Coincident(g20,g21)
    c: Coincident(g708,g709)
    c: Coincident(g920,g921)
    c: Coincident(g705,g706)
    c: Coincident(g712,g713)
    c: Coincident(g937,g938)
    c: Coincident(g728,g729)
    c: Coincident(g701,g702)
    c: Coincident(g938,g939)
    c: Coincident(g36,g39)
    c: Coincident(g21,g22)
    c: Coincident(g919,g920)
    c: Coincident(g956,g957)
    c: Coincident(g948,g950)
    c: Coincident(g949,g951)
    c: Coincident(g955,g957)
    c: Coincident(g939,g940)
    c: Coincident(g706,g707)
    c: Coincident(g946,g948)
    c: Coincident(g950,g952)
    c: Coincident(g713,g714)
    c: Coincident(g729,g730)
    c: Coincident(g919,g942)
    c: Coincident(g727,g728)
    c: Coincident(g700,g701)
    c: Coincident(g707,g708)
    c: Coincident(g962,g963)
    c: Coincident(g963,g964)
    c: Coincident(g721,g722)
    c: Coincident(g961,g962)
    c: Coincident(g699,g700)
    c: Coincident(g944,g946)
    c: Coincident(g964,g965)
    c: Coincident(g720,g721)
    c: Coincident(g940,g941)
    c: Coincident(g714,g715)
    c: Coincident(g717,g718)
    c: Coincident(g698,g699)
    c: Coincident(g720,g730)
    c: Coincident(g941,g942)
    c: Coincident(g947,g949)
    c: Coincident(g960,g961)
    c: Coincident(g958,g965)
    c: Coincident(g718,g719)
    c: Coincident(g715,g716)
    c: Coincident(g943,g944)
    c: Coincident(g768,g769)
    c: Coincident(g769,g770)
    c: Coincident(g887,g888)
    c: Coincident(g886,g887)
    c: Coincident(g697,g698)
    c: Coincident(g959,g960)
    c: Coincident(g958,g959)
    c: Coincident(g763,g764)
    c: Coincident(g716,g717)
    c: Coincident(g882,g883)
    c: Coincident(g762,g763)
    c: Coincident(g883,g884)
    c: Coincident(g945,g947)
    c: Coincident(g767,g768)
    c: Coincident(g888,g889)
    c: Coincident(g885,g886)
    c: Coincident(g943,g945)
    c: Coincident(g911,g912)
    c: Coincident(g770,g771)
    c: Coincident(g764,g765)
    c: Coincident(g696,g697)
    c: Coincident(g881,g882)
    c: Coincident(g884,g885)
    c: Coincident(g761,g762)
    c: Coincident(g24,g25)
    c: Coincident(g32,g33)
    c: Coincident(g744,g745)
    c: Coincident(g745,g746)
    c: Coincident(g696,g719)
    c: Coincident(g25,g26)
    c: Coincident(g32,g35)
    c: Coincident(g771,g772)
    c: Coincident(g914,g915)
    c: Coincident(g765,g766)
    c: Coincident(g880,g881)
    c: Coincident(g760,g761)
    c: Coincident(g912,g913)
    c: Coincident(g739,g740)
    c: Coincident(g738,g739)
    c: Coincident(g766,g767)
    c: Coincident(g889,g890)
    c: Coincident(g743,g744)
    c: Coincident(g746,g747)
    c: Coincident(g879,g880)
    c: Coincident(g740,g741)
    c: Coincident(g772,g773)
    c: Coincident(g759,g760)
    c: Coincident(g913,g914)
    c: Coincident(g737,g738)
    c: Coincident(g890,g891)
    c: Coincident(g878,g879)
    c: Coincident(g747,g748)
    c: Coincident(g28,g29)
    c: Coincident(g29,g30)
    c: Coincident(g877,g878)
    c: Coincident(g891,g892)
    c: Coincident(g758,g759)
    c: Coincident(g741,g742)
    c: Coincident(g736,g737)
    c: Coincident(g742,g743)
    c: Coincident(g876,g877)
    c: Coincident(g916,g917)
    c: Coincident(g915,g916)
    c: Coincident(g37,g38)
    c: Coincident(g20,g23)
    c: Coincident(g845,g846)
    c: Coincident(g824,g825)
    c: Coincident(g773,g774)
    c: Coincident(g892,g893)
    c: Coincident(g748,g749)
    c: Coincident(g735,g736)
    c: Coincident(g910,g911)
    c: Coincident(g757,g758)
    c: Coincident(g875,g876)
    c: Coincident(g908,g909)
    c: Coincident(g825,g826)
    c: Coincident(g844,g845)
    c: Coincident(g907,g908)
    c: Coincident(g909,g910)
    c: Coincident(g792,g793)
    c: Coincident(g22,g23)
    c: Coincident(g38,g39)
    c: Coincident(g823,g824)
    c: Coincident(g846,g847)
    c: Coincident(g893,g894)
    c: Coincident(g865,g866)
    c: Coincident(g840,g841)
    c: Coincident(g819,g820)
    c: Coincident(g863,g865)
    c: Coincident(g917,g918)
    c: Coincident(g793,g794)
    c: Coincident(g776,g777)
    c: Coincident(g841,g842)
    c: Coincident(g818,g819)
    c: Coincident(g734,g735)
    c: Coincident(g874,g875)
    c: Coincident(g906,g907)
    c: Coincident(g820,g821)
    c: Coincident(g839,g840)
    c: Coincident(g774,g775)
    c: Coincident(g791,g792)
    c: Coincident(g894,g895)
    c: Coincident(g756,g757)
    c: Coincident(g787,g788)
    c: Coincident(g786,g787)
    c: Coincident(g843,g844)
    c: Coincident(g826,g827)
    c: Coincident(g777,g778)
    c: Coincident(g874,g897)
    c: Coincident(g788,g789)
    c: Coincident(g867,g873)
    c: Coincident(g749,g750)
    c: Coincident(g842,g843)
    c: Coincident(g901,g902)
    c: Coincident(g817,g818)
    c: Coincident(g733,g734)
    c: Coincident(g902,g903)
    c: Coincident(g872,g873)
    c: Coincident(g775,g776)
    c: Coincident(g821,g822)
    c: Coincident(g822,g823)
    c: Coincident(g838,g839)
    c: Coincident(g847,g848)
    c: Coincident(g794,g795)
    c: Coincident(g905,g906)
    c: Coincident(g871,g872)
    c: Coincident(g895,g896)
    c: Coincident(g785,g786)
    c: Coincident(g755,g756)
    c: Coincident(g898,g918)
    c: Coincident(g752,g753)
    c: Coincident(g789,g790)
    c: Coincident(g790,g791)
    c: Coincident(g816,g817)
    c: Coincident(g827,g828)
    c: Coincident(g837,g838)
    c: Coincident(g750,g751)
    c: Coincident(g732,g733)
    c: Coincident(g848,g849)
    c: Coincident(g755,g778)
    c: Coincident(g896,g897)
    c: Coincident(g795,g796)
    c: Coincident(g784,g785)
    c: Coincident(g815,g816)
    c: Coincident(g900,g901)
    c: Coincident(g814,g815)
    c: Coincident(g904,g905)
    c: Coincident(g753,g754)
    c: Coincident(g903,g904)
    c: Coincident(g836,g837)
    c: Coincident(g828,g829)
    c: Coincident(g829,g830)
    c: Coincident(g751,g752)
    c: Coincident(g849,g850)
    c: Coincident(g783,g784)
    c: Coincident(g830,g831)
    c: Coincident(g796,g797)
    c: Coincident(g812,g813)
    c: Coincident(g835,g836)
    c: Coincident(g898,g899)
    c: Coincident(g813,g814)
    c: Coincident(g731,g732)
    c: Coincident(g899,g900)
    c: Coincident(g811,g812)
    c: Coincident(g782,g783)
    c: Coincident(g834,g835)
    c: Coincident(g731,g754)
    c: Coincident(g870,g871)
    c: Coincident(g850,g851)
    c: Coincident(g803,g831)
    c: Coincident(g810,g811)
    c: Coincident(g869,g870)
    c: Coincident(g864,g866)
    c: Coincident(g868,g869)
    c: Coincident(g833,g834)
    c: Coincident(g781,g782)
    c: Coincident(g797,g798)
    c: Coincident(g807,g808)
    c: Coincident(g867,g868)
    c: Coincident(g861,g863)
    c: Coincident(g851,g852)
    c: Coincident(g806,g807)
    c: Coincident(g859,g861)
    c: Coincident(g862,g864)
    c: Coincident(g809,g810)
    c: Coincident(g860,g862)
    c: Coincident(g780,g781)
    c: Coincident(g852,g853)
    c: Coincident(g856,g857)
    c: Coincident(g832,g833)
    c: Coincident(g798,g799)
    c: Coincident(g857,g859)
    c: Coincident(g24,g27)
    c: Coincident(g33,g34)
    c: Coincident(g808,g809)
    c: Coincident(g803,g804)
    c: Coincident(g853,g854)
    c: Coincident(g800,g801)
    c: Coincident(g26,g27)
    c: Coincident(g34,g35)
    c: Coincident(g832,g855)
    c: Coincident(g805,g806)
    c: Coincident(g799,g800)
    c: Coincident(g804,g805)
    c: Coincident(g779,g780)
    c: Coincident(g854,g855)
    c: Coincident(g801,g802)
    c: Coincident(g858,g860)
    c: Coincident(g856,g858)
    c: Coincident(g779,g802)
    c: Coincident(g28,g31)
    c: Coincident(g30,g31)
FEATURE [PartDesign::Pad] Pad007
  BaseFeature = -> Fillet011
  Direction = (0,0,-1)
  Length = 1.5
  Length2 = 10
  Profile = -> Sketch023
  ReferenceAxis = -> Sketch023 [N_Axis]
  Refine = true
  SideType = 0
  Suppressed = false
  Type = 0
  Type2 = 0
  expr: Length = 1.5
FEATURE [PartDesign::Body] Body022  label="desc_upper_ring"
  AllowCompound = false
  Group = -> [Sketch021,Pad006,Sketch022,Pocket006,PolarPattern005,Fillet010,Fillet011,Sketch023,Pad007]
  Origin = -> Origin036
  Tip = -> Pad007
FEATURE [App::Link] desc_upper_ring
  LinkPlacement = pos=(15.5041,48.0992,187.372) rot=(1,0,0;3.14159rad)
  LinkedObject = -> Body022
  Placement = pos=(15.5041,48.0992,187.372) rot=(1,0,0;3.14159rad)
FEATURE [App::FeaturePython] GroundedJoint  # Assembly grounded joint (typed FeaturePython)
  ObjectToGround = -> Body006
FEATURE [PartDesign::Fillet] Fillet012
  Base = -> Pocket004 [Face5,Face4]
  BaseFeature = -> Pocket004
  Radius = 0.25
  Refine = true
  SupportTransform = false
  Suppressed = false
  UseAllEdges = false
  expr: Radius = 0.25
FEATURE [PartDesign::Body] Body005  label="motor_gear001"
  AllowCompound = false
  Group = -> [InvoluteGear001,Sketch008,Pocket004,Fillet012]
  Origin = -> Origin010
  Placement = pos=(0,0,75) rot=(0,0,1;0rad)
  Tip = -> Fillet012
FEATURE [App::FeaturePython] Joint001  label="Revolute002"  # Assembly joint (typed FeaturePython)
  AngleMax = 0
  AngleMin = 0
  Detach1 = false
  Detach2 = false
  Distance = 0
  Distance2 = 0
  EnableAngleMax = false
  EnableAngleMin = false
  EnableLengthMax = false
  EnableLengthMin = false
  JointType = 1 (Revolute)
  LengthMax = 0
  LengthMin = 0
  Placement1 = pos=(2.47483e-06,9.04337e-05,56) rot=(0,0,1;0rad)
  Placement2 = pos=(34.5,0,1) rot=(0,0,1;0rad)
  Reference1 = -> Assembly [Body019.Face435,Body019.Face435]
  Reference2 = -> Assembly [Body006.Face93,Body006.Edge2]
  Suppressed = false
FEATURE [Assembly::JointGroup] Joints
  Group = -> [GroundedJoint,Joint001]
FEATURE [Assembly::AssemblyObject] Assembly
  Group = -> [Joints,Body006,Body019,motor_gear001,outer_gear,Simulations,Simulation001,Motion001,upper_cover_display,desc_upper_ring,GroundedJoint,Joint001]
  Origin = -> Origin012
  Type = Assembly
FEATURE [Measure::MeasureRadius] Radius  label="Radius: 42.08 mm"
  Element = -> Assembly [outer_gear.PolarPattern.Edge70]
  Radius = 42.0776
FEATURE [Measure::MeasureRadius] Radius001  label="Radius001: 41.39 mm"
  Element = -> Assembly [outer_gear.Fillet004.Edge310]
  Radius = 41.3866
FEATURE [Measure::MeasureDistance] Distance002  label="Distance002: 111.62 mm"
  Distance = 111.62
  DistanceX = 32.2996
  DistanceY = 7.42027
  DistanceZ = 106.586
  Element1 = -> Assembly [upper_cover_display.Pad005.Face3]
  Element2 = -> Assembly [Body006.Fillet.Face6]
  Position1 = (76.0569,-17.9228,118.586)
  Position2 = (43.7572,-10.5025,12)
FEATURE [Measure::MeasureDistance] Distance003  label="Distance003: 108.88 mm"
  Distance = 108.882
  DistanceX = 23.5648
  DistanceY = 77.9815
  DistanceZ = 72.2417
  Element1 = -> Assembly [outer_gear.Fillet004.Edge953]
  Element2 = -> Assembly [Body006.Fillet.Face6]
  Position1 = (-36.5818,121.058,84.2417)
  Position2 = (-13.017,43.0762,12)
FEATURE [Measure::MeasureRadius] Radius002  label="Radius002: 44.29 mm"
  Element = -> Assembly [upper_cover_display.PolarPattern003.Edge29]
  Radius = 44.288
FEATURE [Measure::MeasureRadius] Radius003  label="Radius003: 51.58 mm"
  Element = -> Assembly [outer_gear.Pocket005.Edge312]
  Radius = 51.5776
FEATURE [Measure::MeasureRadius] Radius004  label="Radius004: 42.58 mm"
  Element = -> Assembly [outer_gear.Pocket005.Edge949]
  Radius = 42.5776
FEATURE [App::DocumentObjectGroup] Measurements
  Group = -> [Distance,Distance001,Radius,Radius001,Distance002,Distance003,Radius002,Radius003,Radius004]
